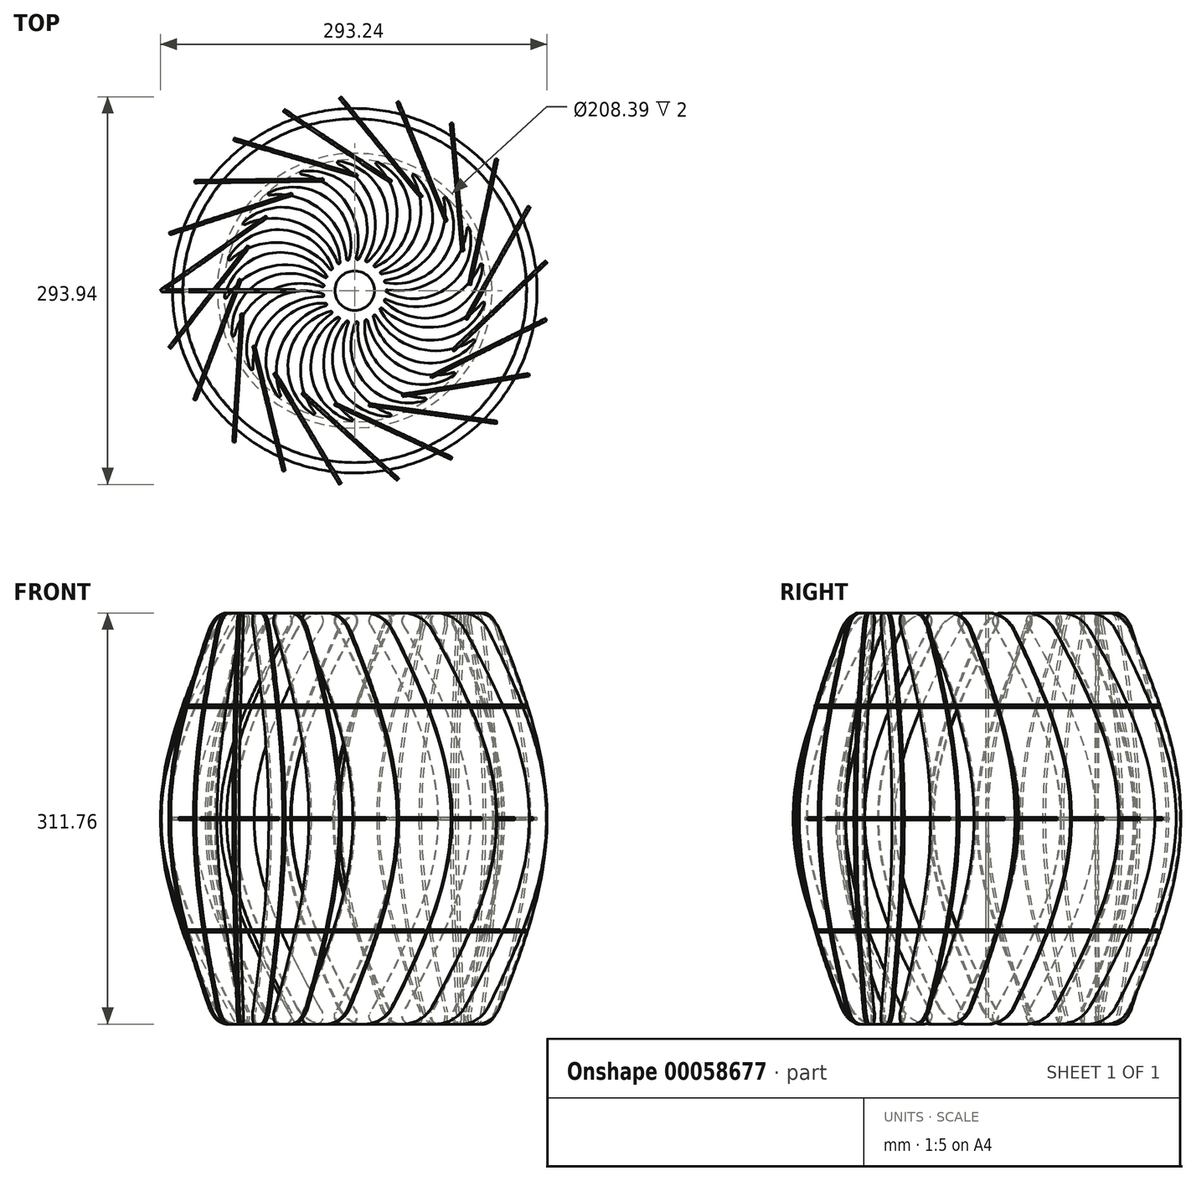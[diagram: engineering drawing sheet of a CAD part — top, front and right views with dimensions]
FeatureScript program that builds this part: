
annotation { "Feature Type Name" : "Feature", "Feature Type Description" : "" }
export const myFeature = defineFeature(function(context is Context, id is Id, definition is map)
    precondition{}
    {
        {
            assignVariable(context, id + "F0", {"name" : "m_thick", "anyValue" : 2 * mm});
        }
        {
            var Q0;
            Q0=qCreatedBy(makeId("Front.planeOp"),FACE);
            var sketch = newSketch(context, id + "F1", { "sketchPlane" : qUnion([Q0])});
            skFitSpline(sketch, "E0", {"points": [v(-90, 155.88) * mm, v(-90, -155.88) * mm], "startDerivative": vector(-227.24, -395.9) * mm, "endDerivative": vector(227.24, -395.9) * mm});
            skFitSpline(sketch, "E1", {"points": [v(-45, 155.88) * mm, v(-45, -155.88) * mm], "startDerivative": vector(-227.24, -395.9) * mm, "endDerivative": vector(227.24, -395.9) * mm});
            skLineSegment(sketch, "E2", {"start": v(0, 0) * mm, "end": v(0, 117.12) * mm, "construction": true});
            skLineSegment(sketch, "E3", {"start": v(0, 117.12) * mm, "end": v(-15, 117.12) * mm, "construction": true});
            skLineSegment(sketch, "E4", {"start": v(-15, 117.12) * mm, "end": v(-15, 84.12) * mm, "construction": true});
            skLineSegment(sketch, "E5", {"start": v(-15, 84.12) * mm, "end": v(0, 84.12) * mm, "construction": true});
            skLineSegment(sketch, "E6", {"start": v(-25, 117.12) * mm, "end": v(-25, 84.12) * mm, "construction": true});
            skLineSegment(sketch, "E7", {"start": v(-90, 155.88) * mm, "end": v(-45, 155.88) * mm});
            skLineSegment(sketch, "E8", {"start": v(-90, -155.88) * mm, "end": v(-45, -155.88) * mm});
            skCircle(sketch, "E9", {"center": v(0, 0) * mm, "radius": 180 * mm, "construction": true});
            skLineSegment(sketch, "E10", {"start": v(0, 0) * mm, "end": v(-293.4, 0) * mm, "construction": true});
            skLineSegment(sketch, "E11.bottom", {"start": v(-15, 84.12) * mm, "end": v(-126.93, 84.12) * mm});
            skLineSegment(sketch, "E11.top", {"start": v(-15, 86.12) * mm, "end": v(-126.93, 86.12) * mm});
            skLineSegment(sketch, "E11.left", {"start": v(-15, 84.12) * mm, "end": v(-15, 86.12) * mm});
            skLineSegment(sketch, "E11.right", {"start": v(-126.93, 84.12) * mm, "end": v(-126.93, 86.12) * mm});
            skLineSegment(sketch, "E12", {"start": v(-104.43, 84.12) * mm, "end": v(-104.43, 86.12) * mm});
            skLineSegment(sketch, "E13", {"start": v(-146.8, 0) * mm, "end": v(-146.8, 76.9) * mm, "construction": true});
            skLineSegment(sketch, "E14.MirrorCS", {"start": v(-15, -84.12) * mm, "end": v(-126.93, -84.12) * mm});
            skLineSegment(sketch, "E15.MirrorCS", {"start": v(-126.93, -84.12) * mm, "end": v(-126.93, -86.12) * mm});
            skLineSegment(sketch, "E16.MirrorCS", {"start": v(-15, -86.12) * mm, "end": v(-126.93, -86.12) * mm});
            skLineSegment(sketch, "E17.MirrorCS", {"start": v(-104.43, -84.12) * mm, "end": v(-104.43, -86.12) * mm});
            skLineSegment(sketch, "E18.MirrorCS", {"start": v(-15, -84.12) * mm, "end": v(-15, -86.12) * mm});
            skLineSegment(sketch, "E19", {"start": v(-124.3, 1) * mm, "end": v(-124.3, -1) * mm});
            skPoint(sketch, "E20", {"position": v(-124.3, 0) * mm});
            skLineSegment(sketch, "E21", {"start": v(-124.3, 1) * mm, "end": v(-101.8, 1) * mm});
            skLineSegment(sketch, "E22", {"start": v(-124.3, -1) * mm, "end": v(-101.8, -1) * mm});
            skSolve(sketch);
        }
        {
            var Q0;
            {var subQ4=sQuery(id+"F1.wireOp",EDGE,"E8");Q0=makeQuery(id+"F1.imprint","IMPRINT",FACE,{"disambiguationData":[TD([[makeQuery(id+"F1.imprint","IMPRINT",EDGE,{"derivedFrom":subQ4}),1.0]])]});}
            var Q1;
            {var subQ5=sQuery(id+"F1.wireOp",EDGE,"E12");Q1=makeQuery(id+"F1.imprint","IMPRINT",FACE,{"disambiguationData":[TD([[makeQuery(id+"F1.imprint","IMPRINT",EDGE,{"derivedFrom":subQ5}),1.0]])]});}
            var Q2;
            {var subQ4=sQuery(id+"F1.wireOp",EDGE,"E7");Q2=makeQuery(id+"F1.imprint","IMPRINT",FACE,{"disambiguationData":[TD([[makeQuery(id+"F1.imprint","IMPRINT",EDGE,{"derivedFrom":subQ4}),-1.0]])]});}
            var Q3;
            {var subQ0=sQuery(id+"F1.wireOp",EDGE,"E11.bottom");var subQ4=sQuery(id+"F1.wireOp",EDGE,"E1");var subQ5=makeQuery(id+"F1.imprint","INTERSECT",VERTEX,{"derivedFrom":[subQ4,subQ0]});Q3=makeQuery(id+"F1.imprint","IMPRINT",FACE,{"disambiguationData":[TD([[makeQuery(id+"F1.imprint","IMPRINT",EDGE,{"disambiguationData":[TD([[subQ5,-1.0]])],"derivedFrom":subQ4}),-1.0]])]});}
            var Q4;
            {var subQ5=sQuery(id+"F1.wireOp",EDGE,"E17.MirrorCS");Q4=makeQuery(id+"F1.imprint","IMPRINT",FACE,{"disambiguationData":[TD([[makeQuery(id+"F1.imprint","IMPRINT",EDGE,{"derivedFrom":subQ5}),-1.0]])]});}
            extrude(context, id + "F2", {"entities" : qUnion([Q0, Q1, Q2, Q3, Q4]), "endBound" : BoundingType.SYMMETRIC, "depth" : getVariable(context, 'm_thick')});
        }
        {
            var Q0;
            Q0=makeQuery(id+"F2.opExtrude","SWEPT_BODY",BODY,{"disambiguationData":[OSD([sQuery(id+"F1.wireOp",EDGE,"E0"),sQuery(id+"F1.wireOp",EDGE,"E1"),sQuery(id+"F1.wireOp",EDGE,"E7"),sQuery(id+"F1.wireOp",EDGE,"E8")])]});
            var Q1;
            Q1=sQuery(id+"F1.wireOp",EDGE,"E13");
            transform(context, id + "F3", {"entities" : qUnion([Q0]), "transformType" : TransformType.ROTATION, "transformAxis" : qUnion([Q1]), "angle" : 35 * degree, "makeCopy" : true});
        }
        {
            var Q0;
            Q0=makeQuery(id+"F3.opPattern","COPY",EDGE,{"derivedFrom":makeQuery(id+"F2.opExtrude","SWEPT_EDGE",EDGE,{"disambiguationData":[OSD([sQuery(id+"F1.wireOp",EDGE,"E1"),sQuery(id+"F1.wireOp",EDGE,"E7")])]}),"instanceName":"1"});
            var Q1;
            Q1=makeQuery(id+"F3.opPattern","COPY",EDGE,{"derivedFrom":makeQuery(id+"F2.opExtrude","SWEPT_EDGE",EDGE,{"disambiguationData":[OSD([sQuery(id+"F1.wireOp",EDGE,"E1"),sQuery(id+"F1.wireOp",EDGE,"E8")])]}),"instanceName":"1"});
            fillet(context, id + "F4", {"entities" : qUnion([Q0, Q1]), "radius" : 6 * mm, "tangentPropagation" : true, "allowEdgeOverflow" : false});
        }
        {
            var Q0;
            Q0=makeQuery(id+"F3.opPattern","COPY",EDGE,{"derivedFrom":makeQuery(id+"F2.opExtrude","SWEPT_EDGE",EDGE,{"disambiguationData":[OSD([sQuery(id+"F1.wireOp",EDGE,"E0"),sQuery(id+"F1.wireOp",EDGE,"E8")])]}),"instanceName":"1"});
            var Q1;
            Q1=makeQuery(id+"F3.opPattern","COPY",EDGE,{"derivedFrom":makeQuery(id+"F2.opExtrude","SWEPT_EDGE",EDGE,{"disambiguationData":[OSD([sQuery(id+"F1.wireOp",EDGE,"E0"),sQuery(id+"F1.wireOp",EDGE,"E7")])]}),"instanceName":"1"});
            fillet(context, id + "F5", {"entities" : qUnion([Q0, Q1]), "radius" : 26.2 * mm, "tangentPropagation" : true, "allowEdgeOverflow" : false});
        }
        {
            var Q0;
            Q0=makeQuery(id+"F3.opPattern","COPY",BODY,{"derivedFrom":makeQuery(id+"F2.opExtrude","SWEPT_BODY",BODY,{"disambiguationData":[OSD([sQuery(id+"F1.wireOp",EDGE,"E0"),sQuery(id+"F1.wireOp",EDGE,"E1"),sQuery(id+"F1.wireOp",EDGE,"E7"),sQuery(id+"F1.wireOp",EDGE,"E8"),sQuery(id+"F1.wireOp",EDGE,"E11.bottom"),sQuery(id+"F1.wireOp",EDGE,"E11.top"),sQuery(id+"F1.wireOp",EDGE,"E12"),sQuery(id+"F1.wireOp",EDGE,"E17.MirrorCS"),sQuery(id+"F1.wireOp",EDGE,"E14.MirrorCS"),sQuery(id+"F1.wireOp",EDGE,"E16.MirrorCS")])]}),"instanceName":"1"});
            var Q1;
            Q1=sQuery(id+"F1.wireOp",EDGE,"E2");
            circularPattern(context, id + "F6", {"entities" : qUnion([Q0]), "axis" : qUnion([Q1]), "angle" : 360 * degree, "instanceCount" : 21, "equalSpace" : true});
        }
        {
            var Q0;
            Q0=qCreatedBy(makeId("Top.planeOp"),FACE);
            var Q1;
            Q1=sQuery(id+"F1.wireOp",VERTEX,"E11.right.start");
            cPlane(context, id + "F7", {"entities" : qUnion([Q0, Q1]), "cplaneType" : CPlaneType.PLANE_POINT, "offset" : 150 * mm, "width" : 150 * mm, "height" : 150 * mm});
        }
        {
            var Q0;
            Q0=qCreatedBy(id+"F7.planeOp",FACE);
            var sketch = newSketch(context, id + "F8", { "sketchPlane" : qUnion([Q0])});
            skCircle(sketch, "E23", {"center": v(0, 0) * mm, "radius": 130.38 * mm});
            skCircle(sketch, "E24", {"center": v(0, 0) * mm, "radius": 15 * mm});
            skCircle(sketch, "E25.0", {"center": v(0, 0) * mm, "radius": 100.38 * mm, "construction": true});
            skCircle(sketch, "E26", {"center": v(0, 0) * mm, "radius": 19 * mm, "construction": true});
            skArc(sketch, "E27", {"start": v(8.33, 23.3) * mm, "mid": v(13.75, 64.38) * mm, "end": v(-12.65, 96.33) * mm});
            skArc(sketch, "E28", {"start": v(9.84, 22.03) * mm, "mid": v(23.2, 67.1) * mm, "end": v(-12.04, 98.21) * mm});
            skPoint(sketch, "E29.visualSharp", {"position": v(-18.15, 98.73) * mm});
            skArc(sketch, "E29.filletArc", {"start": v(-12.04, 98.21) * mm, "mid": v(-13.15, 97.53) * mm, "end": v(-12.65, 96.33) * mm});
            skPoint(sketch, "E30.visualSharp", {"position": v(4.95, 18.35) * mm});
            skArc(sketch, "E30.filletArc", {"start": v(8.33, 23.3) * mm, "mid": v(8.54, 22.02) * mm, "end": v(9.84, 22.03) * mm});
            skArc(sketch, "E31.1.0", {"start": v(1.1, 24.72) * mm, "mid": v(-5.84, 65.58) * mm, "end": v(-40.48, 88.32) * mm});
            skArc(sketch, "E31.1.1", {"start": v(2.91, 23.95) * mm, "mid": v(2.4, 70.96) * mm, "end": v(-40.46, 90.3) * mm});
            skArc(sketch, "E31.1.2", {"start": v(-40.46, 90.3) * mm, "mid": v(-41.31, 89.32) * mm, "end": v(-40.48, 88.32) * mm});
            skArc(sketch, "E31.1.3", {"start": v(1.1, 24.72) * mm, "mid": v(1.68, 23.56) * mm, "end": v(2.91, 23.95) * mm});
            skArc(sketch, "E31.2.0", {"start": v(-6.24, 23.94) * mm, "mid": v(-24.9, 60.94) * mm, "end": v(-64.72, 72.47) * mm});
            skArc(sketch, "E31.2.1", {"start": v(-4.27, 23.74) * mm, "mid": v(-18.62, 68.52) * mm, "end": v(-65.28, 74.36) * mm});
            skArc(sketch, "E31.2.2", {"start": v(-65.28, 74.36) * mm, "mid": v(-65.8, 73.18) * mm, "end": v(-64.72, 72.47) * mm});
            skArc(sketch, "E31.2.3", {"start": v(-6.24, 23.94) * mm, "mid": v(-5.34, 23) * mm, "end": v(-4.27, 23.74) * mm});
            skArc(sketch, "E31.3.0", {"start": v(-13.02, 21.04) * mm, "mid": v(-41.77, 50.9) * mm, "end": v(-83.2, 50.17) * mm});
            skArc(sketch, "E31.3.1", {"start": v(-11.08, 21.43) * mm, "mid": v(-38, 59.98) * mm, "end": v(-84.3, 51.82) * mm});
            skArc(sketch, "E31.3.2", {"start": v(-84.3, 51.82) * mm, "mid": v(-84.45, 50.53) * mm, "end": v(-83.2, 50.17) * mm});
            skArc(sketch, "E31.3.3", {"start": v(-13.02, 21.04) * mm, "mid": v(-11.88, 20.4) * mm, "end": v(-11.08, 21.43) * mm});
            skArc(sketch, "E31.4.0", {"start": v(-18.64, 16.27) * mm, "mid": v(-54.91, 36.32) * mm, "end": v(-94.3, 23.42) * mm});
            skArc(sketch, "E31.4.1", {"start": v(-16.9, 17.21) * mm, "mid": v(-53.98, 46.12) * mm, "end": v(-95.82, 24.67) * mm});
            skArc(sketch, "E31.4.2", {"start": v(-95.82, 24.67) * mm, "mid": v(-95.6, 23.4) * mm, "end": v(-94.3, 23.42) * mm});
            skArc(sketch, "E31.4.3", {"start": v(-18.64, 16.27) * mm, "mid": v(-17.37, 16) * mm, "end": v(-16.9, 17.21) * mm});
            skArc(sketch, "E31.5.0", {"start": v(-22.6, 10.05) * mm, "mid": v(-63.18, 18.52) * mm, "end": v(-97, -5.42) * mm});
            skArc(sketch, "E31.5.1", {"start": v(-21.23, 11.46) * mm, "mid": v(-65.18, 28.16) * mm, "end": v(-98.84, -4.67) * mm});
            skArc(sketch, "E31.5.2", {"start": v(-98.84, -4.67) * mm, "mid": v(-98.24, -5.82) * mm, "end": v(-97, -5.42) * mm});
            skArc(sketch, "E31.5.3", {"start": v(-22.6, 10.05) * mm, "mid": v(-21.32, 10.17) * mm, "end": v(-21.23, 11.46) * mm});
            skArc(sketch, "E31.6.0", {"start": v(-24.57, 2.94) * mm, "mid": v(-65.83, -0.92) * mm, "end": v(-91.1, -33.77) * mm});
            skArc(sketch, "E31.6.1", {"start": v(-23.66, 4.7) * mm, "mid": v(-70.58, 7.7) * mm, "end": v(-93.07, -33.6) * mm});
            skArc(sketch, "E31.6.2", {"start": v(-93.07, -33.6) * mm, "mid": v(-92.16, -34.52) * mm, "end": v(-91.1, -33.77) * mm});
            skArc(sketch, "E31.6.3", {"start": v(-24.57, 2.94) * mm, "mid": v(-23.37, 3.43) * mm, "end": v(-23.66, 4.7) * mm});
            skArc(sketch, "E31.7.0", {"start": v(-24.34, -4.43) * mm, "mid": v(-62.63, -20.29) * mm, "end": v(-77.1, -59.12) * mm});
            skArc(sketch, "E31.7.1", {"start": v(-24, -2.49) * mm, "mid": v(-69.72, -13.45) * mm, "end": v(-79.03, -59.54) * mm});
            skArc(sketch, "E31.7.2", {"start": v(-79.03, -59.54) * mm, "mid": v(-77.89, -60.15) * mm, "end": v(-77.1, -59.12) * mm});
            skArc(sketch, "E31.7.3", {"start": v(-24.34, -4.43) * mm, "mid": v(-23.34, -3.6) * mm, "end": v(-24, -2.49) * mm});
            skArc(sketch, "E31.8.0", {"start": v(-21.95, -11.41) * mm, "mid": v(-53.87, -37.85) * mm, "end": v(-56.25, -79.22) * mm});
            skArc(sketch, "E31.8.1", {"start": v(-22.2, -9.45) * mm, "mid": v(-62.65, -33.4) * mm, "end": v(-57.97, -80.19) * mm});
            skArc(sketch, "E31.8.2", {"start": v(-57.97, -80.19) * mm, "mid": v(-56.7, -80.44) * mm, "end": v(-56.25, -79.22) * mm});
            skArc(sketch, "E31.8.3", {"start": v(-21.95, -11.41) * mm, "mid": v(-21.24, -10.33) * mm, "end": v(-22.2, -9.45) * mm});
            skArc(sketch, "E31.9.0", {"start": v(-17.61, -17.37) * mm, "mid": v(-40.32, -52.04) * mm, "end": v(-30.4, -92.28) * mm});
            skArc(sketch, "E31.9.1", {"start": v(-18.43, -15.57) * mm, "mid": v(-50.02, -50.39) * mm, "end": v(-31.76, -93.71) * mm});
            skArc(sketch, "E31.9.2", {"start": v(-31.76, -93.71) * mm, "mid": v(-30.47, -93.58) * mm, "end": v(-30.4, -92.28) * mm});
            skArc(sketch, "E31.9.3", {"start": v(-17.61, -17.37) * mm, "mid": v(-17.25, -16.13) * mm, "end": v(-18.43, -15.57) * mm});
            skArc(sketch, "E31.10.0", {"start": v(-11.71, -21.8) * mm, "mid": v(-23.2, -61.62) * mm, "end": v(-1.85, -97.14) * mm});
            skArc(sketch, "E31.10.1", {"start": v(-13.02, -20.31) * mm, "mid": v(-32.95, -62.9) * mm, "end": v(-2.73, -98.9) * mm});
            skArc(sketch, "E31.10.2", {"start": v(-2.73, -98.9) * mm, "mid": v(-1.53, -98.4) * mm, "end": v(-1.85, -97.14) * mm});
            skArc(sketch, "E31.10.3", {"start": v(-11.71, -21.8) * mm, "mid": v(-11.73, -20.5) * mm, "end": v(-13.02, -20.31) * mm});
            skArc(sketch, "E31.11.0", {"start": v(-4.77, -24.28) * mm, "mid": v(-4, -65.71) * mm, "end": v(26.87, -93.37) * mm});
            skArc(sketch, "E31.11.1", {"start": v(-6.45, -23.25) * mm, "mid": v(-12.95, -69.81) * mm, "end": v(26.55, -95.32) * mm});
            skArc(sketch, "E31.11.2", {"start": v(26.55, -95.32) * mm, "mid": v(27.54, -94.48) * mm, "end": v(26.87, -93.37) * mm});
            skArc(sketch, "E31.11.3", {"start": v(-4.77, -24.28) * mm, "mid": v(-5.17, -23.04) * mm, "end": v(-6.45, -23.25) * mm});
            skArc(sketch, "E31.12.0", {"start": v(2.6, -24.6) * mm, "mid": v(15.55, -63.97) * mm, "end": v(53.2, -81.3) * mm});
            skArc(sketch, "E31.12.1", {"start": v(0.69, -24.12) * mm, "mid": v(8.2, -70.53) * mm, "end": v(53.46, -83.26) * mm});
            skArc(sketch, "E31.12.2", {"start": v(53.46, -83.26) * mm, "mid": v(54.16, -82.17) * mm, "end": v(53.2, -81.3) * mm});
            skArc(sketch, "E31.12.3", {"start": v(2.6, -24.6) * mm, "mid": v(1.85, -23.54) * mm, "end": v(0.69, -24.12) * mm});
            skArc(sketch, "E31.13.0", {"start": v(9.74, -22.74) * mm, "mid": v(33.71, -56.55) * mm, "end": v(74.8, -62.01) * mm});
            skArc(sketch, "E31.13.1", {"start": v(7.77, -22.84) * mm, "mid": v(28.63, -64.97) * mm, "end": v(75.63, -63.8) * mm});
            skArc(sketch, "E31.13.2", {"start": v(75.63, -63.8) * mm, "mid": v(75.98, -62.55) * mm, "end": v(74.8, -62.01) * mm});
            skArc(sketch, "E31.13.3", {"start": v(9.74, -22.74) * mm, "mid": v(8.71, -21.95) * mm, "end": v(7.77, -22.84) * mm});
            skArc(sketch, "E31.14.0", {"start": v(16, -18.86) * mm, "mid": v(48.88, -44.1) * mm, "end": v(89.75, -37.2) * mm});
            skArc(sketch, "E31.14.1", {"start": v(14.15, -19.54) * mm, "mid": v(46.5, -53.65) * mm, "end": v(91.08, -38.68) * mm});
            skArc(sketch, "E31.14.2", {"start": v(91.08, -38.68) * mm, "mid": v(91.04, -37.38) * mm, "end": v(89.75, -37.2) * mm});
            skArc(sketch, "E31.14.3", {"start": v(16, -18.86) * mm, "mid": v(14.8, -18.4) * mm, "end": v(14.15, -19.54) * mm});
            skArc(sketch, "E31.15.0", {"start": v(20.86, -13.3) * mm, "mid": v(59.71, -27.73) * mm, "end": v(96.73, -9.1) * mm});
            skArc(sketch, "E31.15.1", {"start": v(19.28, -14.5) * mm, "mid": v(60.26, -37.56) * mm, "end": v(98.43, -10.11) * mm});
            skArc(sketch, "E31.15.2", {"start": v(98.43, -10.11) * mm, "mid": v(98.01, -8.88) * mm, "end": v(96.73, -9.1) * mm});
            skArc(sketch, "E31.15.3", {"start": v(20.86, -13.3) * mm, "mid": v(19.56, -13.23) * mm, "end": v(19.28, -14.5) * mm});
            skArc(sketch, "E31.16.0", {"start": v(23.85, -6.57) * mm, "mid": v(65.23, -8.9) * mm, "end": v(95.12, 19.81) * mm});
            skArc(sketch, "E31.16.1", {"start": v(22.7, -8.17) * mm, "mid": v(68.65, -18.13) * mm, "end": v(97.04, 19.35) * mm});
            skArc(sketch, "E31.16.2", {"start": v(97.04, 19.35) * mm, "mid": v(96.27, 20.4) * mm, "end": v(95.12, 19.81) * mm});
            skArc(sketch, "E31.16.3", {"start": v(23.85, -6.57) * mm, "mid": v(22.6, -6.88) * mm, "end": v(22.7, -8.17) * mm});
            skArc(sketch, "E31.17.0", {"start": v(24.73, 0.76) * mm, "mid": v(64.96, 10.72) * mm, "end": v(85.05, 46.97) * mm});
            skArc(sketch, "E31.17.1", {"start": v(24.1, -1.12) * mm, "mid": v(70.94, 2.91) * mm, "end": v(87.02, 47.1) * mm});
            skArc(sketch, "E31.17.2", {"start": v(87.02, 47.1) * mm, "mid": v(85.98, 47.87) * mm, "end": v(85.05, 46.97) * mm});
            skArc(sketch, "E31.17.3", {"start": v(24.73, 0.76) * mm, "mid": v(23.62, 0.09) * mm, "end": v(24.1, -1.12) * mm});
            skArc(sketch, "E31.18.0", {"start": v(23.4, 8.01) * mm, "mid": v(58.91, 29.4) * mm, "end": v(67.43, 69.95) * mm});
            skArc(sketch, "E31.18.1", {"start": v(23.36, 6.04) * mm, "mid": v(66.93, 23.7) * mm, "end": v(69.28, 70.65) * mm});
            skArc(sketch, "E31.18.2", {"start": v(69.28, 70.65) * mm, "mid": v(68.05, 71.1) * mm, "end": v(67.43, 69.95) * mm});
            skArc(sketch, "E31.18.3", {"start": v(23.4, 8.01) * mm, "mid": v(22.54, 7.05) * mm, "end": v(23.36, 6.04) * mm});
            skArc(sketch, "E31.19.0", {"start": v(20, 14.56) * mm, "mid": v(47.63, 45.45) * mm, "end": v(43.81, 86.72) * mm});
            skArc(sketch, "E31.19.1", {"start": v(20.54, 12.65) * mm, "mid": v(56.98, 42.37) * mm, "end": v(45.37, 87.93) * mm});
            skArc(sketch, "E31.19.2", {"start": v(45.37, 87.93) * mm, "mid": v(44.08, 88) * mm, "end": v(43.81, 86.72) * mm});
            skArc(sketch, "E31.19.3", {"start": v(20, 14.56) * mm, "mid": v(19.46, 13.38) * mm, "end": v(20.54, 12.65) * mm});
            skArc(sketch, "E31.20.0", {"start": v(14.83, 19.8) * mm, "mid": v(32.12, 57.47) * mm, "end": v(16.3, 95.78) * mm});
            skArc(sketch, "E31.20.1", {"start": v(15.9, 18.15) * mm, "mid": v(41.96, 57.28) * mm, "end": v(17.44, 97.4) * mm});
            skArc(sketch, "E31.20.2", {"start": v(17.44, 97.4) * mm, "mid": v(16.18, 97.07) * mm, "end": v(16.3, 95.78) * mm});
            skArc(sketch, "E31.20.3", {"start": v(14.83, 19.8) * mm, "mid": v(14.65, 18.52) * mm, "end": v(15.9, 18.15) * mm});
            skSolve(sketch);
        }
        {
            var Q0;
            Q0=makeQuery(id+"F8.imprint","IMPRINT",FACE,{"disambiguationData":[TD([[makeQuery(id+"F8.imprint","IMPRINT",EDGE,{"derivedFrom":sQuery(id+"F8.wireOp",EDGE,"E23")}),1.0]])]});
            extrude(context, id + "F9", {"entities" : qUnion([Q0]), "depth" : getVariable(context, 'm_thick')});
        }
        {
            var Q0;
            Q0=makeQuery(id+"F6.opPattern","COPY",BODY,{"derivedFrom":makeQuery(id+"F3.opPattern","COPY",BODY,{"derivedFrom":makeQuery(id+"F2.opExtrude","SWEPT_BODY",BODY,{"disambiguationData":[OSD([sQuery(id+"F1.wireOp",EDGE,"E0"),sQuery(id+"F1.wireOp",EDGE,"E1"),sQuery(id+"F1.wireOp",EDGE,"E7"),sQuery(id+"F1.wireOp",EDGE,"E8"),sQuery(id+"F1.wireOp",EDGE,"E11.bottom"),sQuery(id+"F1.wireOp",EDGE,"E11.top"),sQuery(id+"F1.wireOp",EDGE,"E12"),sQuery(id+"F1.wireOp",EDGE,"E17.MirrorCS"),sQuery(id+"F1.wireOp",EDGE,"E14.MirrorCS"),sQuery(id+"F1.wireOp",EDGE,"E16.MirrorCS"),sQuery(id+"F1.wireOp",EDGE,"E19"),sQuery(id+"F1.wireOp",EDGE,"E21"),sQuery(id+"F1.wireOp",EDGE,"E22")])]}),"instanceName":"1"}),"instanceName":"2"});
            var Q1;
            Q1=makeQuery(id+"F6.opPattern","COPY",BODY,{"derivedFrom":makeQuery(id+"F3.opPattern","COPY",BODY,{"derivedFrom":makeQuery(id+"F2.opExtrude","SWEPT_BODY",BODY,{"disambiguationData":[OSD([sQuery(id+"F1.wireOp",EDGE,"E0"),sQuery(id+"F1.wireOp",EDGE,"E1"),sQuery(id+"F1.wireOp",EDGE,"E7"),sQuery(id+"F1.wireOp",EDGE,"E8"),sQuery(id+"F1.wireOp",EDGE,"E11.bottom"),sQuery(id+"F1.wireOp",EDGE,"E11.top"),sQuery(id+"F1.wireOp",EDGE,"E12"),sQuery(id+"F1.wireOp",EDGE,"E17.MirrorCS"),sQuery(id+"F1.wireOp",EDGE,"E14.MirrorCS"),sQuery(id+"F1.wireOp",EDGE,"E16.MirrorCS"),sQuery(id+"F1.wireOp",EDGE,"E19"),sQuery(id+"F1.wireOp",EDGE,"E21"),sQuery(id+"F1.wireOp",EDGE,"E22")])]}),"instanceName":"1"}),"instanceName":"3"});
            var Q2;
            Q2=makeQuery(id+"F3.opPattern","COPY",BODY,{"derivedFrom":makeQuery(id+"F2.opExtrude","SWEPT_BODY",BODY,{"disambiguationData":[OSD([sQuery(id+"F1.wireOp",EDGE,"E0"),sQuery(id+"F1.wireOp",EDGE,"E1"),sQuery(id+"F1.wireOp",EDGE,"E7"),sQuery(id+"F1.wireOp",EDGE,"E8"),sQuery(id+"F1.wireOp",EDGE,"E11.bottom"),sQuery(id+"F1.wireOp",EDGE,"E11.top"),sQuery(id+"F1.wireOp",EDGE,"E12"),sQuery(id+"F1.wireOp",EDGE,"E17.MirrorCS"),sQuery(id+"F1.wireOp",EDGE,"E14.MirrorCS"),sQuery(id+"F1.wireOp",EDGE,"E16.MirrorCS"),sQuery(id+"F1.wireOp",EDGE,"E19"),sQuery(id+"F1.wireOp",EDGE,"E21"),sQuery(id+"F1.wireOp",EDGE,"E22")])]}),"instanceName":"1"});
            var Q3;
            Q3=makeQuery(id+"F6.opPattern","COPY",BODY,{"derivedFrom":makeQuery(id+"F3.opPattern","COPY",BODY,{"derivedFrom":makeQuery(id+"F2.opExtrude","SWEPT_BODY",BODY,{"disambiguationData":[OSD([sQuery(id+"F1.wireOp",EDGE,"E0"),sQuery(id+"F1.wireOp",EDGE,"E1"),sQuery(id+"F1.wireOp",EDGE,"E7"),sQuery(id+"F1.wireOp",EDGE,"E8"),sQuery(id+"F1.wireOp",EDGE,"E11.bottom"),sQuery(id+"F1.wireOp",EDGE,"E11.top"),sQuery(id+"F1.wireOp",EDGE,"E12"),sQuery(id+"F1.wireOp",EDGE,"E17.MirrorCS"),sQuery(id+"F1.wireOp",EDGE,"E14.MirrorCS"),sQuery(id+"F1.wireOp",EDGE,"E16.MirrorCS"),sQuery(id+"F1.wireOp",EDGE,"E19"),sQuery(id+"F1.wireOp",EDGE,"E21"),sQuery(id+"F1.wireOp",EDGE,"E22")])]}),"instanceName":"1"}),"instanceName":"1"});
            var Q4;
            Q4=makeQuery(id+"F6.opPattern","COPY",BODY,{"derivedFrom":makeQuery(id+"F3.opPattern","COPY",BODY,{"derivedFrom":makeQuery(id+"F2.opExtrude","SWEPT_BODY",BODY,{"disambiguationData":[OSD([sQuery(id+"F1.wireOp",EDGE,"E0"),sQuery(id+"F1.wireOp",EDGE,"E1"),sQuery(id+"F1.wireOp",EDGE,"E7"),sQuery(id+"F1.wireOp",EDGE,"E8"),sQuery(id+"F1.wireOp",EDGE,"E11.bottom"),sQuery(id+"F1.wireOp",EDGE,"E11.top"),sQuery(id+"F1.wireOp",EDGE,"E12"),sQuery(id+"F1.wireOp",EDGE,"E17.MirrorCS"),sQuery(id+"F1.wireOp",EDGE,"E14.MirrorCS"),sQuery(id+"F1.wireOp",EDGE,"E16.MirrorCS"),sQuery(id+"F1.wireOp",EDGE,"E19"),sQuery(id+"F1.wireOp",EDGE,"E21"),sQuery(id+"F1.wireOp",EDGE,"E22")])]}),"instanceName":"1"}),"instanceName":"4"});
            var Q5;
            Q5=makeQuery(id+"F6.opPattern","COPY",BODY,{"derivedFrom":makeQuery(id+"F3.opPattern","COPY",BODY,{"derivedFrom":makeQuery(id+"F2.opExtrude","SWEPT_BODY",BODY,{"disambiguationData":[OSD([sQuery(id+"F1.wireOp",EDGE,"E0"),sQuery(id+"F1.wireOp",EDGE,"E1"),sQuery(id+"F1.wireOp",EDGE,"E7"),sQuery(id+"F1.wireOp",EDGE,"E8"),sQuery(id+"F1.wireOp",EDGE,"E11.bottom"),sQuery(id+"F1.wireOp",EDGE,"E11.top"),sQuery(id+"F1.wireOp",EDGE,"E12"),sQuery(id+"F1.wireOp",EDGE,"E17.MirrorCS"),sQuery(id+"F1.wireOp",EDGE,"E14.MirrorCS"),sQuery(id+"F1.wireOp",EDGE,"E16.MirrorCS"),sQuery(id+"F1.wireOp",EDGE,"E19"),sQuery(id+"F1.wireOp",EDGE,"E21"),sQuery(id+"F1.wireOp",EDGE,"E22")])]}),"instanceName":"1"}),"instanceName":"20"});
            var Q6;
            Q6=makeQuery(id+"F6.opPattern","COPY",BODY,{"derivedFrom":makeQuery(id+"F3.opPattern","COPY",BODY,{"derivedFrom":makeQuery(id+"F2.opExtrude","SWEPT_BODY",BODY,{"disambiguationData":[OSD([sQuery(id+"F1.wireOp",EDGE,"E0"),sQuery(id+"F1.wireOp",EDGE,"E1"),sQuery(id+"F1.wireOp",EDGE,"E7"),sQuery(id+"F1.wireOp",EDGE,"E8"),sQuery(id+"F1.wireOp",EDGE,"E11.bottom"),sQuery(id+"F1.wireOp",EDGE,"E11.top"),sQuery(id+"F1.wireOp",EDGE,"E12"),sQuery(id+"F1.wireOp",EDGE,"E17.MirrorCS"),sQuery(id+"F1.wireOp",EDGE,"E14.MirrorCS"),sQuery(id+"F1.wireOp",EDGE,"E16.MirrorCS"),sQuery(id+"F1.wireOp",EDGE,"E19"),sQuery(id+"F1.wireOp",EDGE,"E21"),sQuery(id+"F1.wireOp",EDGE,"E22")])]}),"instanceName":"1"}),"instanceName":"5"});
            var Q7;
            Q7=makeQuery(id+"F6.opPattern","COPY",BODY,{"derivedFrom":makeQuery(id+"F3.opPattern","COPY",BODY,{"derivedFrom":makeQuery(id+"F2.opExtrude","SWEPT_BODY",BODY,{"disambiguationData":[OSD([sQuery(id+"F1.wireOp",EDGE,"E0"),sQuery(id+"F1.wireOp",EDGE,"E1"),sQuery(id+"F1.wireOp",EDGE,"E7"),sQuery(id+"F1.wireOp",EDGE,"E8"),sQuery(id+"F1.wireOp",EDGE,"E11.bottom"),sQuery(id+"F1.wireOp",EDGE,"E11.top"),sQuery(id+"F1.wireOp",EDGE,"E12"),sQuery(id+"F1.wireOp",EDGE,"E17.MirrorCS"),sQuery(id+"F1.wireOp",EDGE,"E14.MirrorCS"),sQuery(id+"F1.wireOp",EDGE,"E16.MirrorCS"),sQuery(id+"F1.wireOp",EDGE,"E19"),sQuery(id+"F1.wireOp",EDGE,"E21"),sQuery(id+"F1.wireOp",EDGE,"E22")])]}),"instanceName":"1"}),"instanceName":"6"});
            var Q8;
            Q8=makeQuery(id+"F6.opPattern","COPY",BODY,{"derivedFrom":makeQuery(id+"F3.opPattern","COPY",BODY,{"derivedFrom":makeQuery(id+"F2.opExtrude","SWEPT_BODY",BODY,{"disambiguationData":[OSD([sQuery(id+"F1.wireOp",EDGE,"E0"),sQuery(id+"F1.wireOp",EDGE,"E1"),sQuery(id+"F1.wireOp",EDGE,"E7"),sQuery(id+"F1.wireOp",EDGE,"E8"),sQuery(id+"F1.wireOp",EDGE,"E11.bottom"),sQuery(id+"F1.wireOp",EDGE,"E11.top"),sQuery(id+"F1.wireOp",EDGE,"E12"),sQuery(id+"F1.wireOp",EDGE,"E17.MirrorCS"),sQuery(id+"F1.wireOp",EDGE,"E14.MirrorCS"),sQuery(id+"F1.wireOp",EDGE,"E16.MirrorCS"),sQuery(id+"F1.wireOp",EDGE,"E19"),sQuery(id+"F1.wireOp",EDGE,"E21"),sQuery(id+"F1.wireOp",EDGE,"E22")])]}),"instanceName":"1"}),"instanceName":"19"});
            var Q9;
            Q9=makeQuery(id+"F6.opPattern","COPY",BODY,{"derivedFrom":makeQuery(id+"F3.opPattern","COPY",BODY,{"derivedFrom":makeQuery(id+"F2.opExtrude","SWEPT_BODY",BODY,{"disambiguationData":[OSD([sQuery(id+"F1.wireOp",EDGE,"E0"),sQuery(id+"F1.wireOp",EDGE,"E1"),sQuery(id+"F1.wireOp",EDGE,"E7"),sQuery(id+"F1.wireOp",EDGE,"E8"),sQuery(id+"F1.wireOp",EDGE,"E11.bottom"),sQuery(id+"F1.wireOp",EDGE,"E11.top"),sQuery(id+"F1.wireOp",EDGE,"E12"),sQuery(id+"F1.wireOp",EDGE,"E17.MirrorCS"),sQuery(id+"F1.wireOp",EDGE,"E14.MirrorCS"),sQuery(id+"F1.wireOp",EDGE,"E16.MirrorCS"),sQuery(id+"F1.wireOp",EDGE,"E19"),sQuery(id+"F1.wireOp",EDGE,"E21"),sQuery(id+"F1.wireOp",EDGE,"E22")])]}),"instanceName":"1"}),"instanceName":"18"});
            var Q10;
            Q10=makeQuery(id+"F6.opPattern","COPY",BODY,{"derivedFrom":makeQuery(id+"F3.opPattern","COPY",BODY,{"derivedFrom":makeQuery(id+"F2.opExtrude","SWEPT_BODY",BODY,{"disambiguationData":[OSD([sQuery(id+"F1.wireOp",EDGE,"E0"),sQuery(id+"F1.wireOp",EDGE,"E1"),sQuery(id+"F1.wireOp",EDGE,"E7"),sQuery(id+"F1.wireOp",EDGE,"E8"),sQuery(id+"F1.wireOp",EDGE,"E11.bottom"),sQuery(id+"F1.wireOp",EDGE,"E11.top"),sQuery(id+"F1.wireOp",EDGE,"E12"),sQuery(id+"F1.wireOp",EDGE,"E17.MirrorCS"),sQuery(id+"F1.wireOp",EDGE,"E14.MirrorCS"),sQuery(id+"F1.wireOp",EDGE,"E16.MirrorCS"),sQuery(id+"F1.wireOp",EDGE,"E19"),sQuery(id+"F1.wireOp",EDGE,"E21"),sQuery(id+"F1.wireOp",EDGE,"E22")])]}),"instanceName":"1"}),"instanceName":"7"});
            var Q11;
            Q11=makeQuery(id+"F6.opPattern","COPY",BODY,{"derivedFrom":makeQuery(id+"F3.opPattern","COPY",BODY,{"derivedFrom":makeQuery(id+"F2.opExtrude","SWEPT_BODY",BODY,{"disambiguationData":[OSD([sQuery(id+"F1.wireOp",EDGE,"E0"),sQuery(id+"F1.wireOp",EDGE,"E1"),sQuery(id+"F1.wireOp",EDGE,"E7"),sQuery(id+"F1.wireOp",EDGE,"E8"),sQuery(id+"F1.wireOp",EDGE,"E11.bottom"),sQuery(id+"F1.wireOp",EDGE,"E11.top"),sQuery(id+"F1.wireOp",EDGE,"E12"),sQuery(id+"F1.wireOp",EDGE,"E17.MirrorCS"),sQuery(id+"F1.wireOp",EDGE,"E14.MirrorCS"),sQuery(id+"F1.wireOp",EDGE,"E16.MirrorCS"),sQuery(id+"F1.wireOp",EDGE,"E19"),sQuery(id+"F1.wireOp",EDGE,"E21"),sQuery(id+"F1.wireOp",EDGE,"E22")])]}),"instanceName":"1"}),"instanceName":"17"});
            var Q12;
            Q12=makeQuery(id+"F6.opPattern","COPY",BODY,{"derivedFrom":makeQuery(id+"F3.opPattern","COPY",BODY,{"derivedFrom":makeQuery(id+"F2.opExtrude","SWEPT_BODY",BODY,{"disambiguationData":[OSD([sQuery(id+"F1.wireOp",EDGE,"E0"),sQuery(id+"F1.wireOp",EDGE,"E1"),sQuery(id+"F1.wireOp",EDGE,"E7"),sQuery(id+"F1.wireOp",EDGE,"E8"),sQuery(id+"F1.wireOp",EDGE,"E11.bottom"),sQuery(id+"F1.wireOp",EDGE,"E11.top"),sQuery(id+"F1.wireOp",EDGE,"E12"),sQuery(id+"F1.wireOp",EDGE,"E17.MirrorCS"),sQuery(id+"F1.wireOp",EDGE,"E14.MirrorCS"),sQuery(id+"F1.wireOp",EDGE,"E16.MirrorCS"),sQuery(id+"F1.wireOp",EDGE,"E19"),sQuery(id+"F1.wireOp",EDGE,"E21"),sQuery(id+"F1.wireOp",EDGE,"E22")])]}),"instanceName":"1"}),"instanceName":"16"});
            var Q13;
            Q13=makeQuery(id+"F6.opPattern","COPY",BODY,{"derivedFrom":makeQuery(id+"F3.opPattern","COPY",BODY,{"derivedFrom":makeQuery(id+"F2.opExtrude","SWEPT_BODY",BODY,{"disambiguationData":[OSD([sQuery(id+"F1.wireOp",EDGE,"E0"),sQuery(id+"F1.wireOp",EDGE,"E1"),sQuery(id+"F1.wireOp",EDGE,"E7"),sQuery(id+"F1.wireOp",EDGE,"E8"),sQuery(id+"F1.wireOp",EDGE,"E11.bottom"),sQuery(id+"F1.wireOp",EDGE,"E11.top"),sQuery(id+"F1.wireOp",EDGE,"E12"),sQuery(id+"F1.wireOp",EDGE,"E17.MirrorCS"),sQuery(id+"F1.wireOp",EDGE,"E14.MirrorCS"),sQuery(id+"F1.wireOp",EDGE,"E16.MirrorCS"),sQuery(id+"F1.wireOp",EDGE,"E19"),sQuery(id+"F1.wireOp",EDGE,"E21"),sQuery(id+"F1.wireOp",EDGE,"E22")])]}),"instanceName":"1"}),"instanceName":"15"});
            var Q14;
            Q14=makeQuery(id+"F6.opPattern","COPY",BODY,{"derivedFrom":makeQuery(id+"F3.opPattern","COPY",BODY,{"derivedFrom":makeQuery(id+"F2.opExtrude","SWEPT_BODY",BODY,{"disambiguationData":[OSD([sQuery(id+"F1.wireOp",EDGE,"E0"),sQuery(id+"F1.wireOp",EDGE,"E1"),sQuery(id+"F1.wireOp",EDGE,"E7"),sQuery(id+"F1.wireOp",EDGE,"E8"),sQuery(id+"F1.wireOp",EDGE,"E11.bottom"),sQuery(id+"F1.wireOp",EDGE,"E11.top"),sQuery(id+"F1.wireOp",EDGE,"E12"),sQuery(id+"F1.wireOp",EDGE,"E17.MirrorCS"),sQuery(id+"F1.wireOp",EDGE,"E14.MirrorCS"),sQuery(id+"F1.wireOp",EDGE,"E16.MirrorCS"),sQuery(id+"F1.wireOp",EDGE,"E19"),sQuery(id+"F1.wireOp",EDGE,"E21"),sQuery(id+"F1.wireOp",EDGE,"E22")])]}),"instanceName":"1"}),"instanceName":"8"});
            var Q15;
            Q15=makeQuery(id+"F6.opPattern","COPY",BODY,{"derivedFrom":makeQuery(id+"F3.opPattern","COPY",BODY,{"derivedFrom":makeQuery(id+"F2.opExtrude","SWEPT_BODY",BODY,{"disambiguationData":[OSD([sQuery(id+"F1.wireOp",EDGE,"E0"),sQuery(id+"F1.wireOp",EDGE,"E1"),sQuery(id+"F1.wireOp",EDGE,"E7"),sQuery(id+"F1.wireOp",EDGE,"E8"),sQuery(id+"F1.wireOp",EDGE,"E11.bottom"),sQuery(id+"F1.wireOp",EDGE,"E11.top"),sQuery(id+"F1.wireOp",EDGE,"E12"),sQuery(id+"F1.wireOp",EDGE,"E17.MirrorCS"),sQuery(id+"F1.wireOp",EDGE,"E14.MirrorCS"),sQuery(id+"F1.wireOp",EDGE,"E16.MirrorCS"),sQuery(id+"F1.wireOp",EDGE,"E19"),sQuery(id+"F1.wireOp",EDGE,"E21"),sQuery(id+"F1.wireOp",EDGE,"E22")])]}),"instanceName":"1"}),"instanceName":"9"});
            var Q16;
            Q16=makeQuery(id+"F6.opPattern","COPY",BODY,{"derivedFrom":makeQuery(id+"F3.opPattern","COPY",BODY,{"derivedFrom":makeQuery(id+"F2.opExtrude","SWEPT_BODY",BODY,{"disambiguationData":[OSD([sQuery(id+"F1.wireOp",EDGE,"E0"),sQuery(id+"F1.wireOp",EDGE,"E1"),sQuery(id+"F1.wireOp",EDGE,"E7"),sQuery(id+"F1.wireOp",EDGE,"E8"),sQuery(id+"F1.wireOp",EDGE,"E11.bottom"),sQuery(id+"F1.wireOp",EDGE,"E11.top"),sQuery(id+"F1.wireOp",EDGE,"E12"),sQuery(id+"F1.wireOp",EDGE,"E17.MirrorCS"),sQuery(id+"F1.wireOp",EDGE,"E14.MirrorCS"),sQuery(id+"F1.wireOp",EDGE,"E16.MirrorCS"),sQuery(id+"F1.wireOp",EDGE,"E19"),sQuery(id+"F1.wireOp",EDGE,"E21"),sQuery(id+"F1.wireOp",EDGE,"E22")])]}),"instanceName":"1"}),"instanceName":"10"});
            var Q17;
            Q17=makeQuery(id+"F6.opPattern","COPY",BODY,{"derivedFrom":makeQuery(id+"F3.opPattern","COPY",BODY,{"derivedFrom":makeQuery(id+"F2.opExtrude","SWEPT_BODY",BODY,{"disambiguationData":[OSD([sQuery(id+"F1.wireOp",EDGE,"E0"),sQuery(id+"F1.wireOp",EDGE,"E1"),sQuery(id+"F1.wireOp",EDGE,"E7"),sQuery(id+"F1.wireOp",EDGE,"E8"),sQuery(id+"F1.wireOp",EDGE,"E11.bottom"),sQuery(id+"F1.wireOp",EDGE,"E11.top"),sQuery(id+"F1.wireOp",EDGE,"E12"),sQuery(id+"F1.wireOp",EDGE,"E17.MirrorCS"),sQuery(id+"F1.wireOp",EDGE,"E14.MirrorCS"),sQuery(id+"F1.wireOp",EDGE,"E16.MirrorCS"),sQuery(id+"F1.wireOp",EDGE,"E19"),sQuery(id+"F1.wireOp",EDGE,"E21"),sQuery(id+"F1.wireOp",EDGE,"E22")])]}),"instanceName":"1"}),"instanceName":"11"});
            var Q18;
            Q18=makeQuery(id+"F6.opPattern","COPY",BODY,{"derivedFrom":makeQuery(id+"F3.opPattern","COPY",BODY,{"derivedFrom":makeQuery(id+"F2.opExtrude","SWEPT_BODY",BODY,{"disambiguationData":[OSD([sQuery(id+"F1.wireOp",EDGE,"E0"),sQuery(id+"F1.wireOp",EDGE,"E1"),sQuery(id+"F1.wireOp",EDGE,"E7"),sQuery(id+"F1.wireOp",EDGE,"E8"),sQuery(id+"F1.wireOp",EDGE,"E11.bottom"),sQuery(id+"F1.wireOp",EDGE,"E11.top"),sQuery(id+"F1.wireOp",EDGE,"E12"),sQuery(id+"F1.wireOp",EDGE,"E17.MirrorCS"),sQuery(id+"F1.wireOp",EDGE,"E14.MirrorCS"),sQuery(id+"F1.wireOp",EDGE,"E16.MirrorCS"),sQuery(id+"F1.wireOp",EDGE,"E19"),sQuery(id+"F1.wireOp",EDGE,"E21"),sQuery(id+"F1.wireOp",EDGE,"E22")])]}),"instanceName":"1"}),"instanceName":"14"});
            var Q19;
            Q19=makeQuery(id+"F6.opPattern","COPY",BODY,{"derivedFrom":makeQuery(id+"F3.opPattern","COPY",BODY,{"derivedFrom":makeQuery(id+"F2.opExtrude","SWEPT_BODY",BODY,{"disambiguationData":[OSD([sQuery(id+"F1.wireOp",EDGE,"E0"),sQuery(id+"F1.wireOp",EDGE,"E1"),sQuery(id+"F1.wireOp",EDGE,"E7"),sQuery(id+"F1.wireOp",EDGE,"E8"),sQuery(id+"F1.wireOp",EDGE,"E11.bottom"),sQuery(id+"F1.wireOp",EDGE,"E11.top"),sQuery(id+"F1.wireOp",EDGE,"E12"),sQuery(id+"F1.wireOp",EDGE,"E17.MirrorCS"),sQuery(id+"F1.wireOp",EDGE,"E14.MirrorCS"),sQuery(id+"F1.wireOp",EDGE,"E16.MirrorCS"),sQuery(id+"F1.wireOp",EDGE,"E19"),sQuery(id+"F1.wireOp",EDGE,"E21"),sQuery(id+"F1.wireOp",EDGE,"E22")])]}),"instanceName":"1"}),"instanceName":"13"});
            var Q20;
            Q20=makeQuery(id+"F6.opPattern","COPY",BODY,{"derivedFrom":makeQuery(id+"F3.opPattern","COPY",BODY,{"derivedFrom":makeQuery(id+"F2.opExtrude","SWEPT_BODY",BODY,{"disambiguationData":[OSD([sQuery(id+"F1.wireOp",EDGE,"E0"),sQuery(id+"F1.wireOp",EDGE,"E1"),sQuery(id+"F1.wireOp",EDGE,"E7"),sQuery(id+"F1.wireOp",EDGE,"E8"),sQuery(id+"F1.wireOp",EDGE,"E11.bottom"),sQuery(id+"F1.wireOp",EDGE,"E11.top"),sQuery(id+"F1.wireOp",EDGE,"E12"),sQuery(id+"F1.wireOp",EDGE,"E17.MirrorCS"),sQuery(id+"F1.wireOp",EDGE,"E14.MirrorCS"),sQuery(id+"F1.wireOp",EDGE,"E16.MirrorCS"),sQuery(id+"F1.wireOp",EDGE,"E19"),sQuery(id+"F1.wireOp",EDGE,"E21"),sQuery(id+"F1.wireOp",EDGE,"E22")])]}),"instanceName":"1"}),"instanceName":"12"});
            var Q21;
            Q21=makeQuery(id+"F9.opExtrude","SWEPT_BODY",BODY,{"disambiguationData":[OSD([sQuery(id+"F8.wireOp",EDGE,"E23"),sQuery(id+"F8.wireOp",EDGE,"E24"),sQuery(id+"F8.wireOp",EDGE,"E27"),sQuery(id+"F8.wireOp",EDGE,"E28"),sQuery(id+"F8.wireOp",EDGE,"E29.filletArc"),sQuery(id+"F8.wireOp",EDGE,"E30.filletArc"),sQuery(id+"F8.wireOp",EDGE,"E31.1.0"),sQuery(id+"F8.wireOp",EDGE,"E31.1.1"),sQuery(id+"F8.wireOp",EDGE,"E31.1.2"),sQuery(id+"F8.wireOp",EDGE,"E31.1.3"),sQuery(id+"F8.wireOp",EDGE,"E31.2.0"),sQuery(id+"F8.wireOp",EDGE,"E31.2.1"),sQuery(id+"F8.wireOp",EDGE,"E31.2.2"),sQuery(id+"F8.wireOp",EDGE,"E31.2.3"),sQuery(id+"F8.wireOp",EDGE,"E31.3.0"),sQuery(id+"F8.wireOp",EDGE,"E31.3.1"),sQuery(id+"F8.wireOp",EDGE,"E31.3.2"),sQuery(id+"F8.wireOp",EDGE,"E31.3.3"),sQuery(id+"F8.wireOp",EDGE,"E31.4.0"),sQuery(id+"F8.wireOp",EDGE,"E31.4.1"),sQuery(id+"F8.wireOp",EDGE,"E31.4.2"),sQuery(id+"F8.wireOp",EDGE,"E31.4.3"),sQuery(id+"F8.wireOp",EDGE,"E31.5.0"),sQuery(id+"F8.wireOp",EDGE,"E31.5.1"),sQuery(id+"F8.wireOp",EDGE,"E31.5.2"),sQuery(id+"F8.wireOp",EDGE,"E31.5.3"),sQuery(id+"F8.wireOp",EDGE,"E31.6.0"),sQuery(id+"F8.wireOp",EDGE,"E31.6.1"),sQuery(id+"F8.wireOp",EDGE,"E31.6.2"),sQuery(id+"F8.wireOp",EDGE,"E31.6.3"),sQuery(id+"F8.wireOp",EDGE,"E31.7.0"),sQuery(id+"F8.wireOp",EDGE,"E31.7.1"),sQuery(id+"F8.wireOp",EDGE,"E31.7.2"),sQuery(id+"F8.wireOp",EDGE,"E31.7.3"),sQuery(id+"F8.wireOp",EDGE,"E31.8.0"),sQuery(id+"F8.wireOp",EDGE,"E31.8.1"),sQuery(id+"F8.wireOp",EDGE,"E31.8.2"),sQuery(id+"F8.wireOp",EDGE,"E31.8.3"),sQuery(id+"F8.wireOp",EDGE,"E31.9.0"),sQuery(id+"F8.wireOp",EDGE,"E31.9.1"),sQuery(id+"F8.wireOp",EDGE,"E31.9.2"),sQuery(id+"F8.wireOp",EDGE,"E31.9.3"),sQuery(id+"F8.wireOp",EDGE,"E31.10.0"),sQuery(id+"F8.wireOp",EDGE,"E31.10.1"),sQuery(id+"F8.wireOp",EDGE,"E31.10.2"),sQuery(id+"F8.wireOp",EDGE,"E31.10.3"),sQuery(id+"F8.wireOp",EDGE,"E31.11.0"),sQuery(id+"F8.wireOp",EDGE,"E31.11.1"),sQuery(id+"F8.wireOp",EDGE,"E31.11.2"),sQuery(id+"F8.wireOp",EDGE,"E31.11.3"),sQuery(id+"F8.wireOp",EDGE,"E31.12.0"),sQuery(id+"F8.wireOp",EDGE,"E31.12.1"),sQuery(id+"F8.wireOp",EDGE,"E31.12.2"),sQuery(id+"F8.wireOp",EDGE,"E31.12.3"),sQuery(id+"F8.wireOp",EDGE,"E31.13.0"),sQuery(id+"F8.wireOp",EDGE,"E31.13.1"),sQuery(id+"F8.wireOp",EDGE,"E31.13.2"),sQuery(id+"F8.wireOp",EDGE,"E31.13.3"),sQuery(id+"F8.wireOp",EDGE,"E31.14.0"),sQuery(id+"F8.wireOp",EDGE,"E31.14.1"),sQuery(id+"F8.wireOp",EDGE,"E31.14.2"),sQuery(id+"F8.wireOp",EDGE,"E31.14.3"),sQuery(id+"F8.wireOp",EDGE,"E31.15.0"),sQuery(id+"F8.wireOp",EDGE,"E31.15.1"),sQuery(id+"F8.wireOp",EDGE,"E31.15.2"),sQuery(id+"F8.wireOp",EDGE,"E31.15.3"),sQuery(id+"F8.wireOp",EDGE,"E31.16.0"),sQuery(id+"F8.wireOp",EDGE,"E31.16.1"),sQuery(id+"F8.wireOp",EDGE,"E31.16.2"),sQuery(id+"F8.wireOp",EDGE,"E31.16.3"),sQuery(id+"F8.wireOp",EDGE,"E31.17.0"),sQuery(id+"F8.wireOp",EDGE,"E31.17.1"),sQuery(id+"F8.wireOp",EDGE,"E31.17.2"),sQuery(id+"F8.wireOp",EDGE,"E31.17.3"),sQuery(id+"F8.wireOp",EDGE,"E31.18.0"),sQuery(id+"F8.wireOp",EDGE,"E31.18.1"),sQuery(id+"F8.wireOp",EDGE,"E31.18.2"),sQuery(id+"F8.wireOp",EDGE,"E31.18.3"),sQuery(id+"F8.wireOp",EDGE,"E31.19.0"),sQuery(id+"F8.wireOp",EDGE,"E31.19.1"),sQuery(id+"F8.wireOp",EDGE,"E31.19.2"),sQuery(id+"F8.wireOp",EDGE,"E31.19.3"),sQuery(id+"F8.wireOp",EDGE,"E31.20.0"),sQuery(id+"F8.wireOp",EDGE,"E31.20.1"),sQuery(id+"F8.wireOp",EDGE,"E31.20.2"),sQuery(id+"F8.wireOp",EDGE,"E31.20.3")])]});
            booleanBodies(context, id + "F10", {"operationType" : BooleanOperationType.SUBTRACTION, "tools" : qUnion([Q0, Q1, Q2, Q3, Q4, Q5, Q6, Q7, Q8, Q9, Q10, Q11, Q12, Q13, Q14, Q15, Q16, Q17, Q18, Q19, Q20]), "targets" : qUnion([Q21]), "keepTools" : true});
        }
        {
            var Q0;
            Q0=qCreatedBy(makeId("Top.planeOp"),FACE);
            var Q1;
            Q1=makeQuery(id+"F6.opPattern","COPY",VERTEX,{"derivedFrom":makeQuery(id+"F3.opPattern","COPY",VERTEX,{"derivedFrom":makeQuery(id+"F2.opExtrude","CAP_VERTEX",VERTEX,{"disambiguationData":[OSD([sQuery(id+"F1.wireOp",EDGE,"E1"),sQuery(id+"F1.wireOp",EDGE,"E16.MirrorCS")])],"isStart":false}),"instanceName":"1"}),"instanceName":"8"});
            cPlane(context, id + "F11", {"entities" : qUnion([Q0, Q1]), "cplaneType" : CPlaneType.PLANE_POINT, "offset" : 150 * mm, "width" : 150 * mm, "height" : 150 * mm});
        }
        {
            var Q0;
            Q0=qCreatedBy(id+"F11.planeOp",FACE);
            var sketch = newSketch(context, id + "F12", { "sketchPlane" : qUnion([Q0])});
            skCircle(sketch, "E32", {"center": v(0, 0) * mm, "radius": 129.72 * mm});
            skCircle(sketch, "E33", {"center": v(0, 0) * mm, "radius": 99.48 * mm});
            skSolve(sketch);
        }
        {
            var Q0;
            Q0 = qSketchRegion(id + "F12", true);
            extrude(context, id + "F13", {"entities" : qUnion([Q0]), "depth" : getVariable(context, 'm_thick')});
        }
        {
            var Q0;
            Q0=qCreatedBy(makeId("Top.planeOp"),FACE);
            var sketch = newSketch(context, id + "F14", { "sketchPlane" : qUnion([Q0])});
            skCircle(sketch, "E34", {"center": v(0, 0) * mm, "radius": 146.24 * mm, "construction": true});
            skCircle(sketch, "E35", {"center": v(0, 0) * mm, "radius": 112.2 * mm, "construction": true});
            skCircle(sketch, "E36.0", {"center": v(0, 0) * mm, "radius": 138.24 * mm});
            skCircle(sketch, "E37.0", {"center": v(0, 0) * mm, "radius": 104.2 * mm});
            skSolve(sketch);
        }
        {
            var Q0;
            Q0 = qSketchRegion(id + "F14", true);
            extrude(context, id + "F15", {"entities" : qUnion([Q0]), "endBound" : BoundingType.SYMMETRIC, "depth" : getVariable(context, 'm_thick')});
        }
        {
            var Q0;
            Q0=makeQuery(id+"F6.opPattern","COPY",BODY,{"derivedFrom":makeQuery(id+"F3.opPattern","COPY",BODY,{"derivedFrom":makeQuery(id+"F2.opExtrude","SWEPT_BODY",BODY,{"disambiguationData":[OSD([sQuery(id+"F1.wireOp",EDGE,"E0"),sQuery(id+"F1.wireOp",EDGE,"E1"),sQuery(id+"F1.wireOp",EDGE,"E7"),sQuery(id+"F1.wireOp",EDGE,"E8"),sQuery(id+"F1.wireOp",EDGE,"E11.bottom"),sQuery(id+"F1.wireOp",EDGE,"E11.top"),sQuery(id+"F1.wireOp",EDGE,"E12"),sQuery(id+"F1.wireOp",EDGE,"E17.MirrorCS"),sQuery(id+"F1.wireOp",EDGE,"E14.MirrorCS"),sQuery(id+"F1.wireOp",EDGE,"E16.MirrorCS"),sQuery(id+"F1.wireOp",EDGE,"E19"),sQuery(id+"F1.wireOp",EDGE,"E21"),sQuery(id+"F1.wireOp",EDGE,"E22")])]}),"instanceName":"1"}),"instanceName":"10"});
            var Q1;
            Q1=makeQuery(id+"F6.opPattern","COPY",BODY,{"derivedFrom":makeQuery(id+"F3.opPattern","COPY",BODY,{"derivedFrom":makeQuery(id+"F2.opExtrude","SWEPT_BODY",BODY,{"disambiguationData":[OSD([sQuery(id+"F1.wireOp",EDGE,"E0"),sQuery(id+"F1.wireOp",EDGE,"E1"),sQuery(id+"F1.wireOp",EDGE,"E7"),sQuery(id+"F1.wireOp",EDGE,"E8"),sQuery(id+"F1.wireOp",EDGE,"E11.bottom"),sQuery(id+"F1.wireOp",EDGE,"E11.top"),sQuery(id+"F1.wireOp",EDGE,"E12"),sQuery(id+"F1.wireOp",EDGE,"E17.MirrorCS"),sQuery(id+"F1.wireOp",EDGE,"E14.MirrorCS"),sQuery(id+"F1.wireOp",EDGE,"E16.MirrorCS"),sQuery(id+"F1.wireOp",EDGE,"E19"),sQuery(id+"F1.wireOp",EDGE,"E21"),sQuery(id+"F1.wireOp",EDGE,"E22")])]}),"instanceName":"1"}),"instanceName":"11"});
            var Q2;
            Q2=makeQuery(id+"F6.opPattern","COPY",BODY,{"derivedFrom":makeQuery(id+"F3.opPattern","COPY",BODY,{"derivedFrom":makeQuery(id+"F2.opExtrude","SWEPT_BODY",BODY,{"disambiguationData":[OSD([sQuery(id+"F1.wireOp",EDGE,"E0"),sQuery(id+"F1.wireOp",EDGE,"E1"),sQuery(id+"F1.wireOp",EDGE,"E7"),sQuery(id+"F1.wireOp",EDGE,"E8"),sQuery(id+"F1.wireOp",EDGE,"E11.bottom"),sQuery(id+"F1.wireOp",EDGE,"E11.top"),sQuery(id+"F1.wireOp",EDGE,"E12"),sQuery(id+"F1.wireOp",EDGE,"E17.MirrorCS"),sQuery(id+"F1.wireOp",EDGE,"E14.MirrorCS"),sQuery(id+"F1.wireOp",EDGE,"E16.MirrorCS"),sQuery(id+"F1.wireOp",EDGE,"E19"),sQuery(id+"F1.wireOp",EDGE,"E21"),sQuery(id+"F1.wireOp",EDGE,"E22")])]}),"instanceName":"1"}),"instanceName":"12"});
            var Q3;
            Q3=makeQuery(id+"F6.opPattern","COPY",BODY,{"derivedFrom":makeQuery(id+"F3.opPattern","COPY",BODY,{"derivedFrom":makeQuery(id+"F2.opExtrude","SWEPT_BODY",BODY,{"disambiguationData":[OSD([sQuery(id+"F1.wireOp",EDGE,"E0"),sQuery(id+"F1.wireOp",EDGE,"E1"),sQuery(id+"F1.wireOp",EDGE,"E7"),sQuery(id+"F1.wireOp",EDGE,"E8"),sQuery(id+"F1.wireOp",EDGE,"E11.bottom"),sQuery(id+"F1.wireOp",EDGE,"E11.top"),sQuery(id+"F1.wireOp",EDGE,"E12"),sQuery(id+"F1.wireOp",EDGE,"E17.MirrorCS"),sQuery(id+"F1.wireOp",EDGE,"E14.MirrorCS"),sQuery(id+"F1.wireOp",EDGE,"E16.MirrorCS"),sQuery(id+"F1.wireOp",EDGE,"E19"),sQuery(id+"F1.wireOp",EDGE,"E21"),sQuery(id+"F1.wireOp",EDGE,"E22")])]}),"instanceName":"1"}),"instanceName":"13"});
            var Q4;
            Q4=makeQuery(id+"F6.opPattern","COPY",BODY,{"derivedFrom":makeQuery(id+"F3.opPattern","COPY",BODY,{"derivedFrom":makeQuery(id+"F2.opExtrude","SWEPT_BODY",BODY,{"disambiguationData":[OSD([sQuery(id+"F1.wireOp",EDGE,"E0"),sQuery(id+"F1.wireOp",EDGE,"E1"),sQuery(id+"F1.wireOp",EDGE,"E7"),sQuery(id+"F1.wireOp",EDGE,"E8"),sQuery(id+"F1.wireOp",EDGE,"E11.bottom"),sQuery(id+"F1.wireOp",EDGE,"E11.top"),sQuery(id+"F1.wireOp",EDGE,"E12"),sQuery(id+"F1.wireOp",EDGE,"E17.MirrorCS"),sQuery(id+"F1.wireOp",EDGE,"E14.MirrorCS"),sQuery(id+"F1.wireOp",EDGE,"E16.MirrorCS"),sQuery(id+"F1.wireOp",EDGE,"E19"),sQuery(id+"F1.wireOp",EDGE,"E21"),sQuery(id+"F1.wireOp",EDGE,"E22")])]}),"instanceName":"1"}),"instanceName":"14"});
            var Q5;
            Q5=makeQuery(id+"F6.opPattern","COPY",BODY,{"derivedFrom":makeQuery(id+"F3.opPattern","COPY",BODY,{"derivedFrom":makeQuery(id+"F2.opExtrude","SWEPT_BODY",BODY,{"disambiguationData":[OSD([sQuery(id+"F1.wireOp",EDGE,"E0"),sQuery(id+"F1.wireOp",EDGE,"E1"),sQuery(id+"F1.wireOp",EDGE,"E7"),sQuery(id+"F1.wireOp",EDGE,"E8"),sQuery(id+"F1.wireOp",EDGE,"E11.bottom"),sQuery(id+"F1.wireOp",EDGE,"E11.top"),sQuery(id+"F1.wireOp",EDGE,"E12"),sQuery(id+"F1.wireOp",EDGE,"E17.MirrorCS"),sQuery(id+"F1.wireOp",EDGE,"E14.MirrorCS"),sQuery(id+"F1.wireOp",EDGE,"E16.MirrorCS"),sQuery(id+"F1.wireOp",EDGE,"E19"),sQuery(id+"F1.wireOp",EDGE,"E21"),sQuery(id+"F1.wireOp",EDGE,"E22")])]}),"instanceName":"1"}),"instanceName":"15"});
            var Q6;
            Q6=makeQuery(id+"F6.opPattern","COPY",BODY,{"derivedFrom":makeQuery(id+"F3.opPattern","COPY",BODY,{"derivedFrom":makeQuery(id+"F2.opExtrude","SWEPT_BODY",BODY,{"disambiguationData":[OSD([sQuery(id+"F1.wireOp",EDGE,"E0"),sQuery(id+"F1.wireOp",EDGE,"E1"),sQuery(id+"F1.wireOp",EDGE,"E7"),sQuery(id+"F1.wireOp",EDGE,"E8"),sQuery(id+"F1.wireOp",EDGE,"E11.bottom"),sQuery(id+"F1.wireOp",EDGE,"E11.top"),sQuery(id+"F1.wireOp",EDGE,"E12"),sQuery(id+"F1.wireOp",EDGE,"E17.MirrorCS"),sQuery(id+"F1.wireOp",EDGE,"E14.MirrorCS"),sQuery(id+"F1.wireOp",EDGE,"E16.MirrorCS"),sQuery(id+"F1.wireOp",EDGE,"E19"),sQuery(id+"F1.wireOp",EDGE,"E21"),sQuery(id+"F1.wireOp",EDGE,"E22")])]}),"instanceName":"1"}),"instanceName":"16"});
            var Q7;
            Q7=makeQuery(id+"F6.opPattern","COPY",BODY,{"derivedFrom":makeQuery(id+"F3.opPattern","COPY",BODY,{"derivedFrom":makeQuery(id+"F2.opExtrude","SWEPT_BODY",BODY,{"disambiguationData":[OSD([sQuery(id+"F1.wireOp",EDGE,"E0"),sQuery(id+"F1.wireOp",EDGE,"E1"),sQuery(id+"F1.wireOp",EDGE,"E7"),sQuery(id+"F1.wireOp",EDGE,"E8"),sQuery(id+"F1.wireOp",EDGE,"E11.bottom"),sQuery(id+"F1.wireOp",EDGE,"E11.top"),sQuery(id+"F1.wireOp",EDGE,"E12"),sQuery(id+"F1.wireOp",EDGE,"E17.MirrorCS"),sQuery(id+"F1.wireOp",EDGE,"E14.MirrorCS"),sQuery(id+"F1.wireOp",EDGE,"E16.MirrorCS"),sQuery(id+"F1.wireOp",EDGE,"E19"),sQuery(id+"F1.wireOp",EDGE,"E21"),sQuery(id+"F1.wireOp",EDGE,"E22")])]}),"instanceName":"1"}),"instanceName":"17"});
            var Q8;
            Q8=makeQuery(id+"F6.opPattern","COPY",BODY,{"derivedFrom":makeQuery(id+"F3.opPattern","COPY",BODY,{"derivedFrom":makeQuery(id+"F2.opExtrude","SWEPT_BODY",BODY,{"disambiguationData":[OSD([sQuery(id+"F1.wireOp",EDGE,"E0"),sQuery(id+"F1.wireOp",EDGE,"E1"),sQuery(id+"F1.wireOp",EDGE,"E7"),sQuery(id+"F1.wireOp",EDGE,"E8"),sQuery(id+"F1.wireOp",EDGE,"E11.bottom"),sQuery(id+"F1.wireOp",EDGE,"E11.top"),sQuery(id+"F1.wireOp",EDGE,"E12"),sQuery(id+"F1.wireOp",EDGE,"E17.MirrorCS"),sQuery(id+"F1.wireOp",EDGE,"E14.MirrorCS"),sQuery(id+"F1.wireOp",EDGE,"E16.MirrorCS"),sQuery(id+"F1.wireOp",EDGE,"E19"),sQuery(id+"F1.wireOp",EDGE,"E21"),sQuery(id+"F1.wireOp",EDGE,"E22")])]}),"instanceName":"1"}),"instanceName":"8"});
            var Q9;
            Q9=makeQuery(id+"F6.opPattern","COPY",BODY,{"derivedFrom":makeQuery(id+"F3.opPattern","COPY",BODY,{"derivedFrom":makeQuery(id+"F2.opExtrude","SWEPT_BODY",BODY,{"disambiguationData":[OSD([sQuery(id+"F1.wireOp",EDGE,"E0"),sQuery(id+"F1.wireOp",EDGE,"E1"),sQuery(id+"F1.wireOp",EDGE,"E7"),sQuery(id+"F1.wireOp",EDGE,"E8"),sQuery(id+"F1.wireOp",EDGE,"E11.bottom"),sQuery(id+"F1.wireOp",EDGE,"E11.top"),sQuery(id+"F1.wireOp",EDGE,"E12"),sQuery(id+"F1.wireOp",EDGE,"E17.MirrorCS"),sQuery(id+"F1.wireOp",EDGE,"E14.MirrorCS"),sQuery(id+"F1.wireOp",EDGE,"E16.MirrorCS"),sQuery(id+"F1.wireOp",EDGE,"E19"),sQuery(id+"F1.wireOp",EDGE,"E21"),sQuery(id+"F1.wireOp",EDGE,"E22")])]}),"instanceName":"1"}),"instanceName":"9"});
            var Q10;
            Q10=makeQuery(id+"F6.opPattern","COPY",BODY,{"derivedFrom":makeQuery(id+"F3.opPattern","COPY",BODY,{"derivedFrom":makeQuery(id+"F2.opExtrude","SWEPT_BODY",BODY,{"disambiguationData":[OSD([sQuery(id+"F1.wireOp",EDGE,"E0"),sQuery(id+"F1.wireOp",EDGE,"E1"),sQuery(id+"F1.wireOp",EDGE,"E7"),sQuery(id+"F1.wireOp",EDGE,"E8"),sQuery(id+"F1.wireOp",EDGE,"E11.bottom"),sQuery(id+"F1.wireOp",EDGE,"E11.top"),sQuery(id+"F1.wireOp",EDGE,"E12"),sQuery(id+"F1.wireOp",EDGE,"E17.MirrorCS"),sQuery(id+"F1.wireOp",EDGE,"E14.MirrorCS"),sQuery(id+"F1.wireOp",EDGE,"E16.MirrorCS"),sQuery(id+"F1.wireOp",EDGE,"E19"),sQuery(id+"F1.wireOp",EDGE,"E21"),sQuery(id+"F1.wireOp",EDGE,"E22")])]}),"instanceName":"1"}),"instanceName":"6"});
            var Q11;
            Q11=makeQuery(id+"F6.opPattern","COPY",BODY,{"derivedFrom":makeQuery(id+"F3.opPattern","COPY",BODY,{"derivedFrom":makeQuery(id+"F2.opExtrude","SWEPT_BODY",BODY,{"disambiguationData":[OSD([sQuery(id+"F1.wireOp",EDGE,"E0"),sQuery(id+"F1.wireOp",EDGE,"E1"),sQuery(id+"F1.wireOp",EDGE,"E7"),sQuery(id+"F1.wireOp",EDGE,"E8"),sQuery(id+"F1.wireOp",EDGE,"E11.bottom"),sQuery(id+"F1.wireOp",EDGE,"E11.top"),sQuery(id+"F1.wireOp",EDGE,"E12"),sQuery(id+"F1.wireOp",EDGE,"E17.MirrorCS"),sQuery(id+"F1.wireOp",EDGE,"E14.MirrorCS"),sQuery(id+"F1.wireOp",EDGE,"E16.MirrorCS"),sQuery(id+"F1.wireOp",EDGE,"E19"),sQuery(id+"F1.wireOp",EDGE,"E21"),sQuery(id+"F1.wireOp",EDGE,"E22")])]}),"instanceName":"1"}),"instanceName":"7"});
            var Q12;
            Q12=makeQuery(id+"F6.opPattern","COPY",BODY,{"derivedFrom":makeQuery(id+"F3.opPattern","COPY",BODY,{"derivedFrom":makeQuery(id+"F2.opExtrude","SWEPT_BODY",BODY,{"disambiguationData":[OSD([sQuery(id+"F1.wireOp",EDGE,"E0"),sQuery(id+"F1.wireOp",EDGE,"E1"),sQuery(id+"F1.wireOp",EDGE,"E7"),sQuery(id+"F1.wireOp",EDGE,"E8"),sQuery(id+"F1.wireOp",EDGE,"E11.bottom"),sQuery(id+"F1.wireOp",EDGE,"E11.top"),sQuery(id+"F1.wireOp",EDGE,"E12"),sQuery(id+"F1.wireOp",EDGE,"E17.MirrorCS"),sQuery(id+"F1.wireOp",EDGE,"E14.MirrorCS"),sQuery(id+"F1.wireOp",EDGE,"E16.MirrorCS"),sQuery(id+"F1.wireOp",EDGE,"E19"),sQuery(id+"F1.wireOp",EDGE,"E21"),sQuery(id+"F1.wireOp",EDGE,"E22")])]}),"instanceName":"1"}),"instanceName":"4"});
            var Q13;
            Q13=makeQuery(id+"F6.opPattern","COPY",BODY,{"derivedFrom":makeQuery(id+"F3.opPattern","COPY",BODY,{"derivedFrom":makeQuery(id+"F2.opExtrude","SWEPT_BODY",BODY,{"disambiguationData":[OSD([sQuery(id+"F1.wireOp",EDGE,"E0"),sQuery(id+"F1.wireOp",EDGE,"E1"),sQuery(id+"F1.wireOp",EDGE,"E7"),sQuery(id+"F1.wireOp",EDGE,"E8"),sQuery(id+"F1.wireOp",EDGE,"E11.bottom"),sQuery(id+"F1.wireOp",EDGE,"E11.top"),sQuery(id+"F1.wireOp",EDGE,"E12"),sQuery(id+"F1.wireOp",EDGE,"E17.MirrorCS"),sQuery(id+"F1.wireOp",EDGE,"E14.MirrorCS"),sQuery(id+"F1.wireOp",EDGE,"E16.MirrorCS"),sQuery(id+"F1.wireOp",EDGE,"E19"),sQuery(id+"F1.wireOp",EDGE,"E21"),sQuery(id+"F1.wireOp",EDGE,"E22")])]}),"instanceName":"1"}),"instanceName":"5"});
            var Q14;
            Q14=makeQuery(id+"F6.opPattern","COPY",BODY,{"derivedFrom":makeQuery(id+"F3.opPattern","COPY",BODY,{"derivedFrom":makeQuery(id+"F2.opExtrude","SWEPT_BODY",BODY,{"disambiguationData":[OSD([sQuery(id+"F1.wireOp",EDGE,"E0"),sQuery(id+"F1.wireOp",EDGE,"E1"),sQuery(id+"F1.wireOp",EDGE,"E7"),sQuery(id+"F1.wireOp",EDGE,"E8"),sQuery(id+"F1.wireOp",EDGE,"E11.bottom"),sQuery(id+"F1.wireOp",EDGE,"E11.top"),sQuery(id+"F1.wireOp",EDGE,"E12"),sQuery(id+"F1.wireOp",EDGE,"E17.MirrorCS"),sQuery(id+"F1.wireOp",EDGE,"E14.MirrorCS"),sQuery(id+"F1.wireOp",EDGE,"E16.MirrorCS"),sQuery(id+"F1.wireOp",EDGE,"E19"),sQuery(id+"F1.wireOp",EDGE,"E21"),sQuery(id+"F1.wireOp",EDGE,"E22")])]}),"instanceName":"1"}),"instanceName":"2"});
            var Q15;
            Q15=makeQuery(id+"F6.opPattern","COPY",BODY,{"derivedFrom":makeQuery(id+"F3.opPattern","COPY",BODY,{"derivedFrom":makeQuery(id+"F2.opExtrude","SWEPT_BODY",BODY,{"disambiguationData":[OSD([sQuery(id+"F1.wireOp",EDGE,"E0"),sQuery(id+"F1.wireOp",EDGE,"E1"),sQuery(id+"F1.wireOp",EDGE,"E7"),sQuery(id+"F1.wireOp",EDGE,"E8"),sQuery(id+"F1.wireOp",EDGE,"E11.bottom"),sQuery(id+"F1.wireOp",EDGE,"E11.top"),sQuery(id+"F1.wireOp",EDGE,"E12"),sQuery(id+"F1.wireOp",EDGE,"E17.MirrorCS"),sQuery(id+"F1.wireOp",EDGE,"E14.MirrorCS"),sQuery(id+"F1.wireOp",EDGE,"E16.MirrorCS"),sQuery(id+"F1.wireOp",EDGE,"E19"),sQuery(id+"F1.wireOp",EDGE,"E21"),sQuery(id+"F1.wireOp",EDGE,"E22")])]}),"instanceName":"1"}),"instanceName":"3"});
            var Q16;
            Q16=makeQuery(id+"F6.opPattern","COPY",BODY,{"derivedFrom":makeQuery(id+"F3.opPattern","COPY",BODY,{"derivedFrom":makeQuery(id+"F2.opExtrude","SWEPT_BODY",BODY,{"disambiguationData":[OSD([sQuery(id+"F1.wireOp",EDGE,"E0"),sQuery(id+"F1.wireOp",EDGE,"E1"),sQuery(id+"F1.wireOp",EDGE,"E7"),sQuery(id+"F1.wireOp",EDGE,"E8"),sQuery(id+"F1.wireOp",EDGE,"E11.bottom"),sQuery(id+"F1.wireOp",EDGE,"E11.top"),sQuery(id+"F1.wireOp",EDGE,"E12"),sQuery(id+"F1.wireOp",EDGE,"E17.MirrorCS"),sQuery(id+"F1.wireOp",EDGE,"E14.MirrorCS"),sQuery(id+"F1.wireOp",EDGE,"E16.MirrorCS"),sQuery(id+"F1.wireOp",EDGE,"E19"),sQuery(id+"F1.wireOp",EDGE,"E21"),sQuery(id+"F1.wireOp",EDGE,"E22")])]}),"instanceName":"1"}),"instanceName":"1"});
            var Q17;
            Q17=makeQuery(id+"F3.opPattern","COPY",BODY,{"derivedFrom":makeQuery(id+"F2.opExtrude","SWEPT_BODY",BODY,{"disambiguationData":[OSD([sQuery(id+"F1.wireOp",EDGE,"E0"),sQuery(id+"F1.wireOp",EDGE,"E1"),sQuery(id+"F1.wireOp",EDGE,"E7"),sQuery(id+"F1.wireOp",EDGE,"E8"),sQuery(id+"F1.wireOp",EDGE,"E11.bottom"),sQuery(id+"F1.wireOp",EDGE,"E11.top"),sQuery(id+"F1.wireOp",EDGE,"E12"),sQuery(id+"F1.wireOp",EDGE,"E17.MirrorCS"),sQuery(id+"F1.wireOp",EDGE,"E14.MirrorCS"),sQuery(id+"F1.wireOp",EDGE,"E16.MirrorCS"),sQuery(id+"F1.wireOp",EDGE,"E19"),sQuery(id+"F1.wireOp",EDGE,"E21"),sQuery(id+"F1.wireOp",EDGE,"E22")])]}),"instanceName":"1"});
            var Q18;
            Q18=makeQuery(id+"F6.opPattern","COPY",BODY,{"derivedFrom":makeQuery(id+"F3.opPattern","COPY",BODY,{"derivedFrom":makeQuery(id+"F2.opExtrude","SWEPT_BODY",BODY,{"disambiguationData":[OSD([sQuery(id+"F1.wireOp",EDGE,"E0"),sQuery(id+"F1.wireOp",EDGE,"E1"),sQuery(id+"F1.wireOp",EDGE,"E7"),sQuery(id+"F1.wireOp",EDGE,"E8"),sQuery(id+"F1.wireOp",EDGE,"E11.bottom"),sQuery(id+"F1.wireOp",EDGE,"E11.top"),sQuery(id+"F1.wireOp",EDGE,"E12"),sQuery(id+"F1.wireOp",EDGE,"E17.MirrorCS"),sQuery(id+"F1.wireOp",EDGE,"E14.MirrorCS"),sQuery(id+"F1.wireOp",EDGE,"E16.MirrorCS"),sQuery(id+"F1.wireOp",EDGE,"E19"),sQuery(id+"F1.wireOp",EDGE,"E21"),sQuery(id+"F1.wireOp",EDGE,"E22")])]}),"instanceName":"1"}),"instanceName":"23"});
            var Q19;
            Q19=makeQuery(id+"F6.opPattern","COPY",BODY,{"derivedFrom":makeQuery(id+"F3.opPattern","COPY",BODY,{"derivedFrom":makeQuery(id+"F2.opExtrude","SWEPT_BODY",BODY,{"disambiguationData":[OSD([sQuery(id+"F1.wireOp",EDGE,"E0"),sQuery(id+"F1.wireOp",EDGE,"E1"),sQuery(id+"F1.wireOp",EDGE,"E7"),sQuery(id+"F1.wireOp",EDGE,"E8"),sQuery(id+"F1.wireOp",EDGE,"E11.bottom"),sQuery(id+"F1.wireOp",EDGE,"E11.top"),sQuery(id+"F1.wireOp",EDGE,"E12"),sQuery(id+"F1.wireOp",EDGE,"E17.MirrorCS"),sQuery(id+"F1.wireOp",EDGE,"E14.MirrorCS"),sQuery(id+"F1.wireOp",EDGE,"E16.MirrorCS"),sQuery(id+"F1.wireOp",EDGE,"E19"),sQuery(id+"F1.wireOp",EDGE,"E21"),sQuery(id+"F1.wireOp",EDGE,"E22")])]}),"instanceName":"1"}),"instanceName":"22"});
            var Q20;
            Q20=makeQuery(id+"F6.opPattern","COPY",BODY,{"derivedFrom":makeQuery(id+"F3.opPattern","COPY",BODY,{"derivedFrom":makeQuery(id+"F2.opExtrude","SWEPT_BODY",BODY,{"disambiguationData":[OSD([sQuery(id+"F1.wireOp",EDGE,"E0"),sQuery(id+"F1.wireOp",EDGE,"E1"),sQuery(id+"F1.wireOp",EDGE,"E7"),sQuery(id+"F1.wireOp",EDGE,"E8"),sQuery(id+"F1.wireOp",EDGE,"E11.bottom"),sQuery(id+"F1.wireOp",EDGE,"E11.top"),sQuery(id+"F1.wireOp",EDGE,"E12"),sQuery(id+"F1.wireOp",EDGE,"E17.MirrorCS"),sQuery(id+"F1.wireOp",EDGE,"E14.MirrorCS"),sQuery(id+"F1.wireOp",EDGE,"E16.MirrorCS"),sQuery(id+"F1.wireOp",EDGE,"E19"),sQuery(id+"F1.wireOp",EDGE,"E21"),sQuery(id+"F1.wireOp",EDGE,"E22")])]}),"instanceName":"1"}),"instanceName":"27"});
            var Q21;
            Q21=makeQuery(id+"F6.opPattern","COPY",BODY,{"derivedFrom":makeQuery(id+"F3.opPattern","COPY",BODY,{"derivedFrom":makeQuery(id+"F2.opExtrude","SWEPT_BODY",BODY,{"disambiguationData":[OSD([sQuery(id+"F1.wireOp",EDGE,"E0"),sQuery(id+"F1.wireOp",EDGE,"E1"),sQuery(id+"F1.wireOp",EDGE,"E7"),sQuery(id+"F1.wireOp",EDGE,"E8"),sQuery(id+"F1.wireOp",EDGE,"E11.bottom"),sQuery(id+"F1.wireOp",EDGE,"E11.top"),sQuery(id+"F1.wireOp",EDGE,"E12"),sQuery(id+"F1.wireOp",EDGE,"E17.MirrorCS"),sQuery(id+"F1.wireOp",EDGE,"E14.MirrorCS"),sQuery(id+"F1.wireOp",EDGE,"E16.MirrorCS"),sQuery(id+"F1.wireOp",EDGE,"E19"),sQuery(id+"F1.wireOp",EDGE,"E21"),sQuery(id+"F1.wireOp",EDGE,"E22")])]}),"instanceName":"1"}),"instanceName":"25"});
            var Q22;
            Q22=makeQuery(id+"F6.opPattern","COPY",BODY,{"derivedFrom":makeQuery(id+"F3.opPattern","COPY",BODY,{"derivedFrom":makeQuery(id+"F2.opExtrude","SWEPT_BODY",BODY,{"disambiguationData":[OSD([sQuery(id+"F1.wireOp",EDGE,"E0"),sQuery(id+"F1.wireOp",EDGE,"E1"),sQuery(id+"F1.wireOp",EDGE,"E7"),sQuery(id+"F1.wireOp",EDGE,"E8"),sQuery(id+"F1.wireOp",EDGE,"E11.bottom"),sQuery(id+"F1.wireOp",EDGE,"E11.top"),sQuery(id+"F1.wireOp",EDGE,"E12"),sQuery(id+"F1.wireOp",EDGE,"E17.MirrorCS"),sQuery(id+"F1.wireOp",EDGE,"E14.MirrorCS"),sQuery(id+"F1.wireOp",EDGE,"E16.MirrorCS"),sQuery(id+"F1.wireOp",EDGE,"E19"),sQuery(id+"F1.wireOp",EDGE,"E21"),sQuery(id+"F1.wireOp",EDGE,"E22")])]}),"instanceName":"1"}),"instanceName":"20"});
            var Q23;
            Q23=makeQuery(id+"F6.opPattern","COPY",BODY,{"derivedFrom":makeQuery(id+"F3.opPattern","COPY",BODY,{"derivedFrom":makeQuery(id+"F2.opExtrude","SWEPT_BODY",BODY,{"disambiguationData":[OSD([sQuery(id+"F1.wireOp",EDGE,"E0"),sQuery(id+"F1.wireOp",EDGE,"E1"),sQuery(id+"F1.wireOp",EDGE,"E7"),sQuery(id+"F1.wireOp",EDGE,"E8"),sQuery(id+"F1.wireOp",EDGE,"E11.bottom"),sQuery(id+"F1.wireOp",EDGE,"E11.top"),sQuery(id+"F1.wireOp",EDGE,"E12"),sQuery(id+"F1.wireOp",EDGE,"E17.MirrorCS"),sQuery(id+"F1.wireOp",EDGE,"E14.MirrorCS"),sQuery(id+"F1.wireOp",EDGE,"E16.MirrorCS"),sQuery(id+"F1.wireOp",EDGE,"E19"),sQuery(id+"F1.wireOp",EDGE,"E21"),sQuery(id+"F1.wireOp",EDGE,"E22")])]}),"instanceName":"1"}),"instanceName":"24"});
            var Q24;
            Q24=makeQuery(id+"F6.opPattern","COPY",BODY,{"derivedFrom":makeQuery(id+"F3.opPattern","COPY",BODY,{"derivedFrom":makeQuery(id+"F2.opExtrude","SWEPT_BODY",BODY,{"disambiguationData":[OSD([sQuery(id+"F1.wireOp",EDGE,"E0"),sQuery(id+"F1.wireOp",EDGE,"E1"),sQuery(id+"F1.wireOp",EDGE,"E7"),sQuery(id+"F1.wireOp",EDGE,"E8"),sQuery(id+"F1.wireOp",EDGE,"E11.bottom"),sQuery(id+"F1.wireOp",EDGE,"E11.top"),sQuery(id+"F1.wireOp",EDGE,"E12"),sQuery(id+"F1.wireOp",EDGE,"E17.MirrorCS"),sQuery(id+"F1.wireOp",EDGE,"E14.MirrorCS"),sQuery(id+"F1.wireOp",EDGE,"E16.MirrorCS"),sQuery(id+"F1.wireOp",EDGE,"E19"),sQuery(id+"F1.wireOp",EDGE,"E21"),sQuery(id+"F1.wireOp",EDGE,"E22")])]}),"instanceName":"1"}),"instanceName":"18"});
            var Q25;
            Q25=makeQuery(id+"F6.opPattern","COPY",BODY,{"derivedFrom":makeQuery(id+"F3.opPattern","COPY",BODY,{"derivedFrom":makeQuery(id+"F2.opExtrude","SWEPT_BODY",BODY,{"disambiguationData":[OSD([sQuery(id+"F1.wireOp",EDGE,"E0"),sQuery(id+"F1.wireOp",EDGE,"E1"),sQuery(id+"F1.wireOp",EDGE,"E7"),sQuery(id+"F1.wireOp",EDGE,"E8"),sQuery(id+"F1.wireOp",EDGE,"E11.bottom"),sQuery(id+"F1.wireOp",EDGE,"E11.top"),sQuery(id+"F1.wireOp",EDGE,"E12"),sQuery(id+"F1.wireOp",EDGE,"E17.MirrorCS"),sQuery(id+"F1.wireOp",EDGE,"E14.MirrorCS"),sQuery(id+"F1.wireOp",EDGE,"E16.MirrorCS"),sQuery(id+"F1.wireOp",EDGE,"E19"),sQuery(id+"F1.wireOp",EDGE,"E21"),sQuery(id+"F1.wireOp",EDGE,"E22")])]}),"instanceName":"1"}),"instanceName":"21"});
            var Q26;
            Q26=makeQuery(id+"F6.opPattern","COPY",BODY,{"derivedFrom":makeQuery(id+"F3.opPattern","COPY",BODY,{"derivedFrom":makeQuery(id+"F2.opExtrude","SWEPT_BODY",BODY,{"disambiguationData":[OSD([sQuery(id+"F1.wireOp",EDGE,"E0"),sQuery(id+"F1.wireOp",EDGE,"E1"),sQuery(id+"F1.wireOp",EDGE,"E7"),sQuery(id+"F1.wireOp",EDGE,"E8"),sQuery(id+"F1.wireOp",EDGE,"E11.bottom"),sQuery(id+"F1.wireOp",EDGE,"E11.top"),sQuery(id+"F1.wireOp",EDGE,"E12"),sQuery(id+"F1.wireOp",EDGE,"E17.MirrorCS"),sQuery(id+"F1.wireOp",EDGE,"E14.MirrorCS"),sQuery(id+"F1.wireOp",EDGE,"E16.MirrorCS"),sQuery(id+"F1.wireOp",EDGE,"E19"),sQuery(id+"F1.wireOp",EDGE,"E21"),sQuery(id+"F1.wireOp",EDGE,"E22")])]}),"instanceName":"1"}),"instanceName":"26"});
            var Q27;
            Q27=makeQuery(id+"F6.opPattern","COPY",BODY,{"derivedFrom":makeQuery(id+"F3.opPattern","COPY",BODY,{"derivedFrom":makeQuery(id+"F2.opExtrude","SWEPT_BODY",BODY,{"disambiguationData":[OSD([sQuery(id+"F1.wireOp",EDGE,"E0"),sQuery(id+"F1.wireOp",EDGE,"E1"),sQuery(id+"F1.wireOp",EDGE,"E7"),sQuery(id+"F1.wireOp",EDGE,"E8"),sQuery(id+"F1.wireOp",EDGE,"E11.bottom"),sQuery(id+"F1.wireOp",EDGE,"E11.top"),sQuery(id+"F1.wireOp",EDGE,"E12"),sQuery(id+"F1.wireOp",EDGE,"E17.MirrorCS"),sQuery(id+"F1.wireOp",EDGE,"E14.MirrorCS"),sQuery(id+"F1.wireOp",EDGE,"E16.MirrorCS"),sQuery(id+"F1.wireOp",EDGE,"E19"),sQuery(id+"F1.wireOp",EDGE,"E21"),sQuery(id+"F1.wireOp",EDGE,"E22")])]}),"instanceName":"1"}),"instanceName":"19"});
            var Q28;
            Q28=makeQuery(id+"F13.opExtrude","SWEPT_BODY",BODY,{"disambiguationData":[OSD([sQuery(id+"F12.wireOp",EDGE,"E32"),sQuery(id+"F12.wireOp",EDGE,"E33")])]});
            booleanBodies(context, id + "F16", {"operationType" : BooleanOperationType.SUBTRACTION, "tools" : qUnion([Q0, Q1, Q2, Q3, Q4, Q5, Q6, Q7, Q8, Q9, Q10, Q11, Q12, Q13, Q14, Q15, Q16, Q17, Q18, Q19, Q20, Q21, Q22, Q23, Q24, Q25, Q26, Q27]), "targets" : qUnion([Q28]), "keepTools" : true});
        }
        {
            var Q0;
            Q0=makeQuery(id+"F6.opPattern","COPY",BODY,{"derivedFrom":makeQuery(id+"F3.opPattern","COPY",BODY,{"derivedFrom":makeQuery(id+"F2.opExtrude","SWEPT_BODY",BODY,{"disambiguationData":[OSD([sQuery(id+"F1.wireOp",EDGE,"E0"),sQuery(id+"F1.wireOp",EDGE,"E1"),sQuery(id+"F1.wireOp",EDGE,"E7"),sQuery(id+"F1.wireOp",EDGE,"E8"),sQuery(id+"F1.wireOp",EDGE,"E11.bottom"),sQuery(id+"F1.wireOp",EDGE,"E11.top"),sQuery(id+"F1.wireOp",EDGE,"E12"),sQuery(id+"F1.wireOp",EDGE,"E17.MirrorCS"),sQuery(id+"F1.wireOp",EDGE,"E14.MirrorCS"),sQuery(id+"F1.wireOp",EDGE,"E16.MirrorCS"),sQuery(id+"F1.wireOp",EDGE,"E19"),sQuery(id+"F1.wireOp",EDGE,"E21"),sQuery(id+"F1.wireOp",EDGE,"E22")])]}),"instanceName":"1"}),"instanceName":"1"});
            var Q1;
            Q1=makeQuery(id+"F6.opPattern","COPY",BODY,{"derivedFrom":makeQuery(id+"F3.opPattern","COPY",BODY,{"derivedFrom":makeQuery(id+"F2.opExtrude","SWEPT_BODY",BODY,{"disambiguationData":[OSD([sQuery(id+"F1.wireOp",EDGE,"E0"),sQuery(id+"F1.wireOp",EDGE,"E1"),sQuery(id+"F1.wireOp",EDGE,"E7"),sQuery(id+"F1.wireOp",EDGE,"E8"),sQuery(id+"F1.wireOp",EDGE,"E11.bottom"),sQuery(id+"F1.wireOp",EDGE,"E11.top"),sQuery(id+"F1.wireOp",EDGE,"E12"),sQuery(id+"F1.wireOp",EDGE,"E17.MirrorCS"),sQuery(id+"F1.wireOp",EDGE,"E14.MirrorCS"),sQuery(id+"F1.wireOp",EDGE,"E16.MirrorCS"),sQuery(id+"F1.wireOp",EDGE,"E19"),sQuery(id+"F1.wireOp",EDGE,"E21"),sQuery(id+"F1.wireOp",EDGE,"E22")])]}),"instanceName":"1"}),"instanceName":"2"});
            var Q2;
            Q2=makeQuery(id+"F3.opPattern","COPY",BODY,{"derivedFrom":makeQuery(id+"F2.opExtrude","SWEPT_BODY",BODY,{"disambiguationData":[OSD([sQuery(id+"F1.wireOp",EDGE,"E0"),sQuery(id+"F1.wireOp",EDGE,"E1"),sQuery(id+"F1.wireOp",EDGE,"E7"),sQuery(id+"F1.wireOp",EDGE,"E8"),sQuery(id+"F1.wireOp",EDGE,"E11.bottom"),sQuery(id+"F1.wireOp",EDGE,"E11.top"),sQuery(id+"F1.wireOp",EDGE,"E12"),sQuery(id+"F1.wireOp",EDGE,"E17.MirrorCS"),sQuery(id+"F1.wireOp",EDGE,"E14.MirrorCS"),sQuery(id+"F1.wireOp",EDGE,"E16.MirrorCS"),sQuery(id+"F1.wireOp",EDGE,"E19"),sQuery(id+"F1.wireOp",EDGE,"E21"),sQuery(id+"F1.wireOp",EDGE,"E22")])]}),"instanceName":"1"});
            var Q3;
            Q3=makeQuery(id+"F6.opPattern","COPY",BODY,{"derivedFrom":makeQuery(id+"F3.opPattern","COPY",BODY,{"derivedFrom":makeQuery(id+"F2.opExtrude","SWEPT_BODY",BODY,{"disambiguationData":[OSD([sQuery(id+"F1.wireOp",EDGE,"E0"),sQuery(id+"F1.wireOp",EDGE,"E1"),sQuery(id+"F1.wireOp",EDGE,"E7"),sQuery(id+"F1.wireOp",EDGE,"E8"),sQuery(id+"F1.wireOp",EDGE,"E11.bottom"),sQuery(id+"F1.wireOp",EDGE,"E11.top"),sQuery(id+"F1.wireOp",EDGE,"E12"),sQuery(id+"F1.wireOp",EDGE,"E17.MirrorCS"),sQuery(id+"F1.wireOp",EDGE,"E14.MirrorCS"),sQuery(id+"F1.wireOp",EDGE,"E16.MirrorCS"),sQuery(id+"F1.wireOp",EDGE,"E19"),sQuery(id+"F1.wireOp",EDGE,"E21"),sQuery(id+"F1.wireOp",EDGE,"E22")])]}),"instanceName":"1"}),"instanceName":"20"});
            var Q4;
            Q4=makeQuery(id+"F6.opPattern","COPY",BODY,{"derivedFrom":makeQuery(id+"F3.opPattern","COPY",BODY,{"derivedFrom":makeQuery(id+"F2.opExtrude","SWEPT_BODY",BODY,{"disambiguationData":[OSD([sQuery(id+"F1.wireOp",EDGE,"E0"),sQuery(id+"F1.wireOp",EDGE,"E1"),sQuery(id+"F1.wireOp",EDGE,"E7"),sQuery(id+"F1.wireOp",EDGE,"E8"),sQuery(id+"F1.wireOp",EDGE,"E11.bottom"),sQuery(id+"F1.wireOp",EDGE,"E11.top"),sQuery(id+"F1.wireOp",EDGE,"E12"),sQuery(id+"F1.wireOp",EDGE,"E17.MirrorCS"),sQuery(id+"F1.wireOp",EDGE,"E14.MirrorCS"),sQuery(id+"F1.wireOp",EDGE,"E16.MirrorCS"),sQuery(id+"F1.wireOp",EDGE,"E19"),sQuery(id+"F1.wireOp",EDGE,"E21"),sQuery(id+"F1.wireOp",EDGE,"E22")])]}),"instanceName":"1"}),"instanceName":"19"});
            var Q5;
            Q5=makeQuery(id+"F6.opPattern","COPY",BODY,{"derivedFrom":makeQuery(id+"F3.opPattern","COPY",BODY,{"derivedFrom":makeQuery(id+"F2.opExtrude","SWEPT_BODY",BODY,{"disambiguationData":[OSD([sQuery(id+"F1.wireOp",EDGE,"E0"),sQuery(id+"F1.wireOp",EDGE,"E1"),sQuery(id+"F1.wireOp",EDGE,"E7"),sQuery(id+"F1.wireOp",EDGE,"E8"),sQuery(id+"F1.wireOp",EDGE,"E11.bottom"),sQuery(id+"F1.wireOp",EDGE,"E11.top"),sQuery(id+"F1.wireOp",EDGE,"E12"),sQuery(id+"F1.wireOp",EDGE,"E17.MirrorCS"),sQuery(id+"F1.wireOp",EDGE,"E14.MirrorCS"),sQuery(id+"F1.wireOp",EDGE,"E16.MirrorCS"),sQuery(id+"F1.wireOp",EDGE,"E19"),sQuery(id+"F1.wireOp",EDGE,"E21"),sQuery(id+"F1.wireOp",EDGE,"E22")])]}),"instanceName":"1"}),"instanceName":"18"});
            var Q6;
            Q6=makeQuery(id+"F6.opPattern","COPY",BODY,{"derivedFrom":makeQuery(id+"F3.opPattern","COPY",BODY,{"derivedFrom":makeQuery(id+"F2.opExtrude","SWEPT_BODY",BODY,{"disambiguationData":[OSD([sQuery(id+"F1.wireOp",EDGE,"E0"),sQuery(id+"F1.wireOp",EDGE,"E1"),sQuery(id+"F1.wireOp",EDGE,"E7"),sQuery(id+"F1.wireOp",EDGE,"E8"),sQuery(id+"F1.wireOp",EDGE,"E11.bottom"),sQuery(id+"F1.wireOp",EDGE,"E11.top"),sQuery(id+"F1.wireOp",EDGE,"E12"),sQuery(id+"F1.wireOp",EDGE,"E17.MirrorCS"),sQuery(id+"F1.wireOp",EDGE,"E14.MirrorCS"),sQuery(id+"F1.wireOp",EDGE,"E16.MirrorCS"),sQuery(id+"F1.wireOp",EDGE,"E19"),sQuery(id+"F1.wireOp",EDGE,"E21"),sQuery(id+"F1.wireOp",EDGE,"E22")])]}),"instanceName":"1"}),"instanceName":"17"});
            var Q7;
            Q7=makeQuery(id+"F6.opPattern","COPY",BODY,{"derivedFrom":makeQuery(id+"F3.opPattern","COPY",BODY,{"derivedFrom":makeQuery(id+"F2.opExtrude","SWEPT_BODY",BODY,{"disambiguationData":[OSD([sQuery(id+"F1.wireOp",EDGE,"E0"),sQuery(id+"F1.wireOp",EDGE,"E1"),sQuery(id+"F1.wireOp",EDGE,"E7"),sQuery(id+"F1.wireOp",EDGE,"E8"),sQuery(id+"F1.wireOp",EDGE,"E11.bottom"),sQuery(id+"F1.wireOp",EDGE,"E11.top"),sQuery(id+"F1.wireOp",EDGE,"E12"),sQuery(id+"F1.wireOp",EDGE,"E17.MirrorCS"),sQuery(id+"F1.wireOp",EDGE,"E14.MirrorCS"),sQuery(id+"F1.wireOp",EDGE,"E16.MirrorCS"),sQuery(id+"F1.wireOp",EDGE,"E19"),sQuery(id+"F1.wireOp",EDGE,"E21"),sQuery(id+"F1.wireOp",EDGE,"E22")])]}),"instanceName":"1"}),"instanceName":"3"});
            var Q8;
            Q8=makeQuery(id+"F6.opPattern","COPY",BODY,{"derivedFrom":makeQuery(id+"F3.opPattern","COPY",BODY,{"derivedFrom":makeQuery(id+"F2.opExtrude","SWEPT_BODY",BODY,{"disambiguationData":[OSD([sQuery(id+"F1.wireOp",EDGE,"E0"),sQuery(id+"F1.wireOp",EDGE,"E1"),sQuery(id+"F1.wireOp",EDGE,"E7"),sQuery(id+"F1.wireOp",EDGE,"E8"),sQuery(id+"F1.wireOp",EDGE,"E11.bottom"),sQuery(id+"F1.wireOp",EDGE,"E11.top"),sQuery(id+"F1.wireOp",EDGE,"E12"),sQuery(id+"F1.wireOp",EDGE,"E17.MirrorCS"),sQuery(id+"F1.wireOp",EDGE,"E14.MirrorCS"),sQuery(id+"F1.wireOp",EDGE,"E16.MirrorCS"),sQuery(id+"F1.wireOp",EDGE,"E19"),sQuery(id+"F1.wireOp",EDGE,"E21"),sQuery(id+"F1.wireOp",EDGE,"E22")])]}),"instanceName":"1"}),"instanceName":"16"});
            var Q9;
            Q9=makeQuery(id+"F6.opPattern","COPY",BODY,{"derivedFrom":makeQuery(id+"F3.opPattern","COPY",BODY,{"derivedFrom":makeQuery(id+"F2.opExtrude","SWEPT_BODY",BODY,{"disambiguationData":[OSD([sQuery(id+"F1.wireOp",EDGE,"E0"),sQuery(id+"F1.wireOp",EDGE,"E1"),sQuery(id+"F1.wireOp",EDGE,"E7"),sQuery(id+"F1.wireOp",EDGE,"E8"),sQuery(id+"F1.wireOp",EDGE,"E11.bottom"),sQuery(id+"F1.wireOp",EDGE,"E11.top"),sQuery(id+"F1.wireOp",EDGE,"E12"),sQuery(id+"F1.wireOp",EDGE,"E17.MirrorCS"),sQuery(id+"F1.wireOp",EDGE,"E14.MirrorCS"),sQuery(id+"F1.wireOp",EDGE,"E16.MirrorCS"),sQuery(id+"F1.wireOp",EDGE,"E19"),sQuery(id+"F1.wireOp",EDGE,"E21"),sQuery(id+"F1.wireOp",EDGE,"E22")])]}),"instanceName":"1"}),"instanceName":"4"});
            var Q10;
            Q10=makeQuery(id+"F6.opPattern","COPY",BODY,{"derivedFrom":makeQuery(id+"F3.opPattern","COPY",BODY,{"derivedFrom":makeQuery(id+"F2.opExtrude","SWEPT_BODY",BODY,{"disambiguationData":[OSD([sQuery(id+"F1.wireOp",EDGE,"E0"),sQuery(id+"F1.wireOp",EDGE,"E1"),sQuery(id+"F1.wireOp",EDGE,"E7"),sQuery(id+"F1.wireOp",EDGE,"E8"),sQuery(id+"F1.wireOp",EDGE,"E11.bottom"),sQuery(id+"F1.wireOp",EDGE,"E11.top"),sQuery(id+"F1.wireOp",EDGE,"E12"),sQuery(id+"F1.wireOp",EDGE,"E17.MirrorCS"),sQuery(id+"F1.wireOp",EDGE,"E14.MirrorCS"),sQuery(id+"F1.wireOp",EDGE,"E16.MirrorCS"),sQuery(id+"F1.wireOp",EDGE,"E19"),sQuery(id+"F1.wireOp",EDGE,"E21"),sQuery(id+"F1.wireOp",EDGE,"E22")])]}),"instanceName":"1"}),"instanceName":"5"});
            var Q11;
            Q11=makeQuery(id+"F6.opPattern","COPY",BODY,{"derivedFrom":makeQuery(id+"F3.opPattern","COPY",BODY,{"derivedFrom":makeQuery(id+"F2.opExtrude","SWEPT_BODY",BODY,{"disambiguationData":[OSD([sQuery(id+"F1.wireOp",EDGE,"E0"),sQuery(id+"F1.wireOp",EDGE,"E1"),sQuery(id+"F1.wireOp",EDGE,"E7"),sQuery(id+"F1.wireOp",EDGE,"E8"),sQuery(id+"F1.wireOp",EDGE,"E11.bottom"),sQuery(id+"F1.wireOp",EDGE,"E11.top"),sQuery(id+"F1.wireOp",EDGE,"E12"),sQuery(id+"F1.wireOp",EDGE,"E17.MirrorCS"),sQuery(id+"F1.wireOp",EDGE,"E14.MirrorCS"),sQuery(id+"F1.wireOp",EDGE,"E16.MirrorCS"),sQuery(id+"F1.wireOp",EDGE,"E19"),sQuery(id+"F1.wireOp",EDGE,"E21"),sQuery(id+"F1.wireOp",EDGE,"E22")])]}),"instanceName":"1"}),"instanceName":"15"});
            var Q12;
            Q12=makeQuery(id+"F6.opPattern","COPY",BODY,{"derivedFrom":makeQuery(id+"F3.opPattern","COPY",BODY,{"derivedFrom":makeQuery(id+"F2.opExtrude","SWEPT_BODY",BODY,{"disambiguationData":[OSD([sQuery(id+"F1.wireOp",EDGE,"E0"),sQuery(id+"F1.wireOp",EDGE,"E1"),sQuery(id+"F1.wireOp",EDGE,"E7"),sQuery(id+"F1.wireOp",EDGE,"E8"),sQuery(id+"F1.wireOp",EDGE,"E11.bottom"),sQuery(id+"F1.wireOp",EDGE,"E11.top"),sQuery(id+"F1.wireOp",EDGE,"E12"),sQuery(id+"F1.wireOp",EDGE,"E17.MirrorCS"),sQuery(id+"F1.wireOp",EDGE,"E14.MirrorCS"),sQuery(id+"F1.wireOp",EDGE,"E16.MirrorCS"),sQuery(id+"F1.wireOp",EDGE,"E19"),sQuery(id+"F1.wireOp",EDGE,"E21"),sQuery(id+"F1.wireOp",EDGE,"E22")])]}),"instanceName":"1"}),"instanceName":"6"});
            var Q13;
            Q13=makeQuery(id+"F6.opPattern","COPY",BODY,{"derivedFrom":makeQuery(id+"F3.opPattern","COPY",BODY,{"derivedFrom":makeQuery(id+"F2.opExtrude","SWEPT_BODY",BODY,{"disambiguationData":[OSD([sQuery(id+"F1.wireOp",EDGE,"E0"),sQuery(id+"F1.wireOp",EDGE,"E1"),sQuery(id+"F1.wireOp",EDGE,"E7"),sQuery(id+"F1.wireOp",EDGE,"E8"),sQuery(id+"F1.wireOp",EDGE,"E11.bottom"),sQuery(id+"F1.wireOp",EDGE,"E11.top"),sQuery(id+"F1.wireOp",EDGE,"E12"),sQuery(id+"F1.wireOp",EDGE,"E17.MirrorCS"),sQuery(id+"F1.wireOp",EDGE,"E14.MirrorCS"),sQuery(id+"F1.wireOp",EDGE,"E16.MirrorCS"),sQuery(id+"F1.wireOp",EDGE,"E19"),sQuery(id+"F1.wireOp",EDGE,"E21"),sQuery(id+"F1.wireOp",EDGE,"E22")])]}),"instanceName":"1"}),"instanceName":"14"});
            var Q14;
            Q14=makeQuery(id+"F6.opPattern","COPY",BODY,{"derivedFrom":makeQuery(id+"F3.opPattern","COPY",BODY,{"derivedFrom":makeQuery(id+"F2.opExtrude","SWEPT_BODY",BODY,{"disambiguationData":[OSD([sQuery(id+"F1.wireOp",EDGE,"E0"),sQuery(id+"F1.wireOp",EDGE,"E1"),sQuery(id+"F1.wireOp",EDGE,"E7"),sQuery(id+"F1.wireOp",EDGE,"E8"),sQuery(id+"F1.wireOp",EDGE,"E11.bottom"),sQuery(id+"F1.wireOp",EDGE,"E11.top"),sQuery(id+"F1.wireOp",EDGE,"E12"),sQuery(id+"F1.wireOp",EDGE,"E17.MirrorCS"),sQuery(id+"F1.wireOp",EDGE,"E14.MirrorCS"),sQuery(id+"F1.wireOp",EDGE,"E16.MirrorCS"),sQuery(id+"F1.wireOp",EDGE,"E19"),sQuery(id+"F1.wireOp",EDGE,"E21"),sQuery(id+"F1.wireOp",EDGE,"E22")])]}),"instanceName":"1"}),"instanceName":"13"});
            var Q15;
            Q15=makeQuery(id+"F6.opPattern","COPY",BODY,{"derivedFrom":makeQuery(id+"F3.opPattern","COPY",BODY,{"derivedFrom":makeQuery(id+"F2.opExtrude","SWEPT_BODY",BODY,{"disambiguationData":[OSD([sQuery(id+"F1.wireOp",EDGE,"E0"),sQuery(id+"F1.wireOp",EDGE,"E1"),sQuery(id+"F1.wireOp",EDGE,"E7"),sQuery(id+"F1.wireOp",EDGE,"E8"),sQuery(id+"F1.wireOp",EDGE,"E11.bottom"),sQuery(id+"F1.wireOp",EDGE,"E11.top"),sQuery(id+"F1.wireOp",EDGE,"E12"),sQuery(id+"F1.wireOp",EDGE,"E17.MirrorCS"),sQuery(id+"F1.wireOp",EDGE,"E14.MirrorCS"),sQuery(id+"F1.wireOp",EDGE,"E16.MirrorCS"),sQuery(id+"F1.wireOp",EDGE,"E19"),sQuery(id+"F1.wireOp",EDGE,"E21"),sQuery(id+"F1.wireOp",EDGE,"E22")])]}),"instanceName":"1"}),"instanceName":"7"});
            var Q16;
            Q16=makeQuery(id+"F6.opPattern","COPY",BODY,{"derivedFrom":makeQuery(id+"F3.opPattern","COPY",BODY,{"derivedFrom":makeQuery(id+"F2.opExtrude","SWEPT_BODY",BODY,{"disambiguationData":[OSD([sQuery(id+"F1.wireOp",EDGE,"E0"),sQuery(id+"F1.wireOp",EDGE,"E1"),sQuery(id+"F1.wireOp",EDGE,"E7"),sQuery(id+"F1.wireOp",EDGE,"E8"),sQuery(id+"F1.wireOp",EDGE,"E11.bottom"),sQuery(id+"F1.wireOp",EDGE,"E11.top"),sQuery(id+"F1.wireOp",EDGE,"E12"),sQuery(id+"F1.wireOp",EDGE,"E17.MirrorCS"),sQuery(id+"F1.wireOp",EDGE,"E14.MirrorCS"),sQuery(id+"F1.wireOp",EDGE,"E16.MirrorCS"),sQuery(id+"F1.wireOp",EDGE,"E19"),sQuery(id+"F1.wireOp",EDGE,"E21"),sQuery(id+"F1.wireOp",EDGE,"E22")])]}),"instanceName":"1"}),"instanceName":"8"});
            var Q17;
            Q17=makeQuery(id+"F6.opPattern","COPY",BODY,{"derivedFrom":makeQuery(id+"F3.opPattern","COPY",BODY,{"derivedFrom":makeQuery(id+"F2.opExtrude","SWEPT_BODY",BODY,{"disambiguationData":[OSD([sQuery(id+"F1.wireOp",EDGE,"E0"),sQuery(id+"F1.wireOp",EDGE,"E1"),sQuery(id+"F1.wireOp",EDGE,"E7"),sQuery(id+"F1.wireOp",EDGE,"E8"),sQuery(id+"F1.wireOp",EDGE,"E11.bottom"),sQuery(id+"F1.wireOp",EDGE,"E11.top"),sQuery(id+"F1.wireOp",EDGE,"E12"),sQuery(id+"F1.wireOp",EDGE,"E17.MirrorCS"),sQuery(id+"F1.wireOp",EDGE,"E14.MirrorCS"),sQuery(id+"F1.wireOp",EDGE,"E16.MirrorCS"),sQuery(id+"F1.wireOp",EDGE,"E19"),sQuery(id+"F1.wireOp",EDGE,"E21"),sQuery(id+"F1.wireOp",EDGE,"E22")])]}),"instanceName":"1"}),"instanceName":"9"});
            var Q18;
            Q18=makeQuery(id+"F6.opPattern","COPY",BODY,{"derivedFrom":makeQuery(id+"F3.opPattern","COPY",BODY,{"derivedFrom":makeQuery(id+"F2.opExtrude","SWEPT_BODY",BODY,{"disambiguationData":[OSD([sQuery(id+"F1.wireOp",EDGE,"E0"),sQuery(id+"F1.wireOp",EDGE,"E1"),sQuery(id+"F1.wireOp",EDGE,"E7"),sQuery(id+"F1.wireOp",EDGE,"E8"),sQuery(id+"F1.wireOp",EDGE,"E11.bottom"),sQuery(id+"F1.wireOp",EDGE,"E11.top"),sQuery(id+"F1.wireOp",EDGE,"E12"),sQuery(id+"F1.wireOp",EDGE,"E17.MirrorCS"),sQuery(id+"F1.wireOp",EDGE,"E14.MirrorCS"),sQuery(id+"F1.wireOp",EDGE,"E16.MirrorCS"),sQuery(id+"F1.wireOp",EDGE,"E19"),sQuery(id+"F1.wireOp",EDGE,"E21"),sQuery(id+"F1.wireOp",EDGE,"E22")])]}),"instanceName":"1"}),"instanceName":"10"});
            var Q19;
            Q19=makeQuery(id+"F6.opPattern","COPY",BODY,{"derivedFrom":makeQuery(id+"F3.opPattern","COPY",BODY,{"derivedFrom":makeQuery(id+"F2.opExtrude","SWEPT_BODY",BODY,{"disambiguationData":[OSD([sQuery(id+"F1.wireOp",EDGE,"E0"),sQuery(id+"F1.wireOp",EDGE,"E1"),sQuery(id+"F1.wireOp",EDGE,"E7"),sQuery(id+"F1.wireOp",EDGE,"E8"),sQuery(id+"F1.wireOp",EDGE,"E11.bottom"),sQuery(id+"F1.wireOp",EDGE,"E11.top"),sQuery(id+"F1.wireOp",EDGE,"E12"),sQuery(id+"F1.wireOp",EDGE,"E17.MirrorCS"),sQuery(id+"F1.wireOp",EDGE,"E14.MirrorCS"),sQuery(id+"F1.wireOp",EDGE,"E16.MirrorCS"),sQuery(id+"F1.wireOp",EDGE,"E19"),sQuery(id+"F1.wireOp",EDGE,"E21"),sQuery(id+"F1.wireOp",EDGE,"E22")])]}),"instanceName":"1"}),"instanceName":"11"});
            var Q20;
            Q20=makeQuery(id+"F6.opPattern","COPY",BODY,{"derivedFrom":makeQuery(id+"F3.opPattern","COPY",BODY,{"derivedFrom":makeQuery(id+"F2.opExtrude","SWEPT_BODY",BODY,{"disambiguationData":[OSD([sQuery(id+"F1.wireOp",EDGE,"E0"),sQuery(id+"F1.wireOp",EDGE,"E1"),sQuery(id+"F1.wireOp",EDGE,"E7"),sQuery(id+"F1.wireOp",EDGE,"E8"),sQuery(id+"F1.wireOp",EDGE,"E11.bottom"),sQuery(id+"F1.wireOp",EDGE,"E11.top"),sQuery(id+"F1.wireOp",EDGE,"E12"),sQuery(id+"F1.wireOp",EDGE,"E17.MirrorCS"),sQuery(id+"F1.wireOp",EDGE,"E14.MirrorCS"),sQuery(id+"F1.wireOp",EDGE,"E16.MirrorCS"),sQuery(id+"F1.wireOp",EDGE,"E19"),sQuery(id+"F1.wireOp",EDGE,"E21"),sQuery(id+"F1.wireOp",EDGE,"E22")])]}),"instanceName":"1"}),"instanceName":"12"});
            var Q21;
            Q21=makeQuery(id+"F15.opExtrude","SWEPT_BODY",BODY,{"disambiguationData":[OSD([sQuery(id+"F14.wireOp",EDGE,"E36.0"),sQuery(id+"F14.wireOp",EDGE,"E37.0")])]});
            booleanBodies(context, id + "F17", {"operationType" : BooleanOperationType.SUBTRACTION, "tools" : qUnion([Q0, Q1, Q2, Q3, Q4, Q5, Q6, Q7, Q8, Q9, Q10, Q11, Q12, Q13, Q14, Q15, Q16, Q17, Q18, Q19, Q20]), "targets" : qUnion([Q21]), "keepTools" : true});
        }
    });
